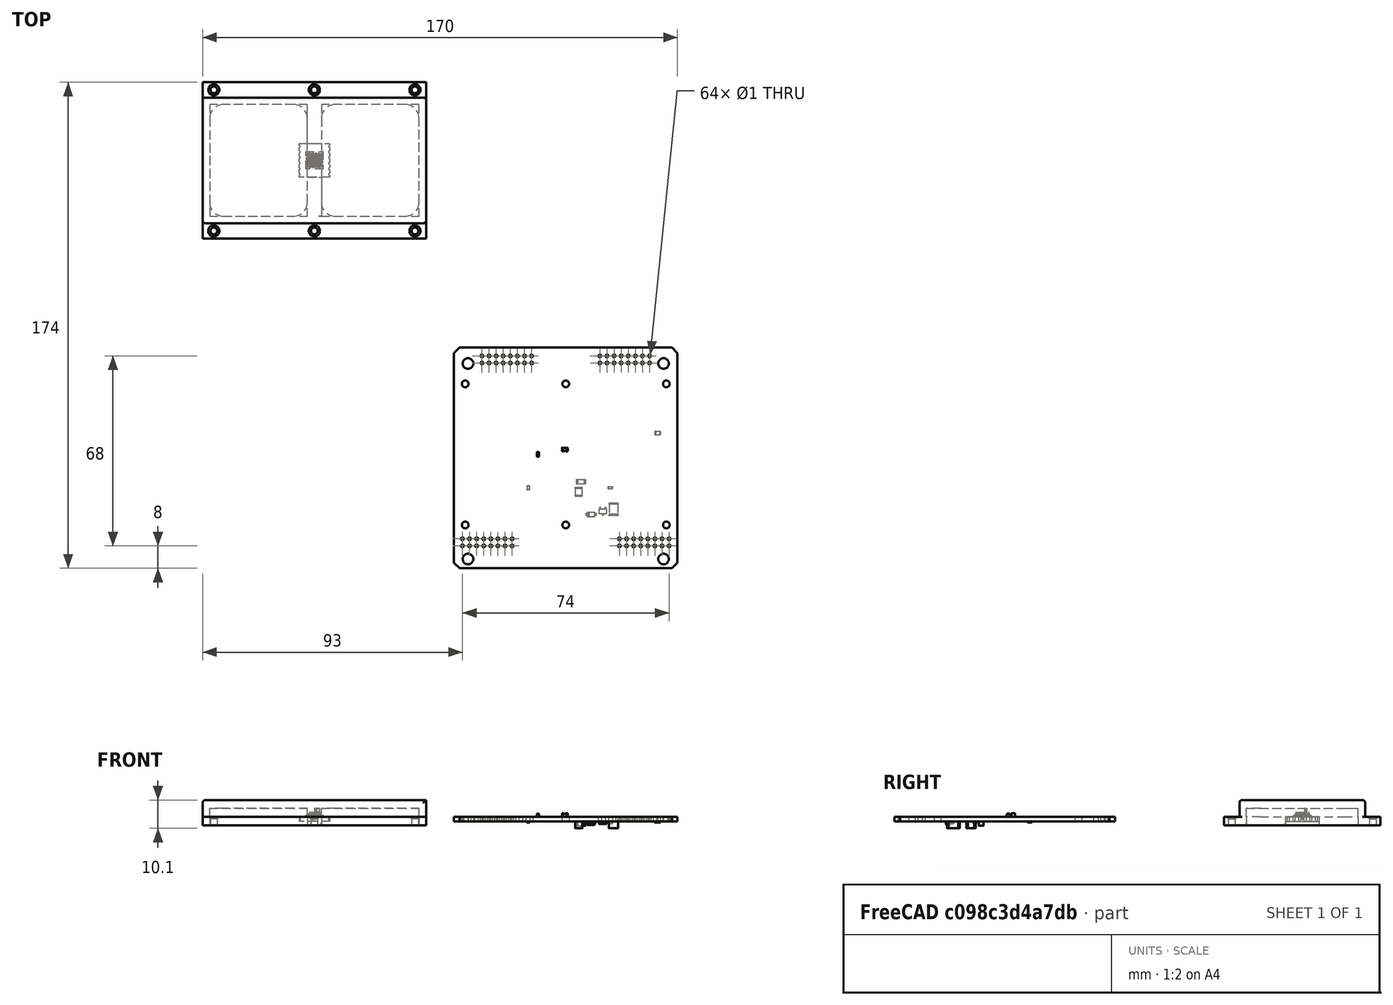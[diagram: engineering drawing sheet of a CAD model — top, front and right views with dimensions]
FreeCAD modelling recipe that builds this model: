
FCSTD DOCUMENT  (FreeCAD 0.21R33771 (Git))
Label: Modelo3DV2
License: All rights reserved
LicenseURL: http://en.wikipedia.org/wiki/All_rights_reserved
objects: Part::Feature×268, App::Link×148, App::Part×28, PartDesign::CoordinateSystem×1, Sketcher::SketchObject×1
note: 270 computed .brp shape members not serialized (recipe doc carries the construction recipe); baked Part::Feature solids carry a one-line shape summary decoded from their .brp

FEATURE [PartDesign::CoordinateSystem] Local_CS_d980
  AttacherType = Attacher::AttachEngine3D
  MapMode = 2
  Support = -> [X_Axis001]
FEATURE [Part::Feature] Pcb_d980
  shape: bbox 80 x 79 x 1.6 mm, 84 faces (baked)
FEATURE [Sketcher::SketchObject] PCB_Sketch_d980
  FullyConstrained = false
  sketch-geometry (12):
    g0: LineSegment StartX=52 StartY=-146 StartZ=0 EndX=50 EndY=-144 EndZ=0
    g1: LineSegment StartX=50 StartY=-69 StartZ=0 EndX=52 EndY=-67 EndZ=0
    g2: LineSegment StartX=50 StartY=-144 StartZ=0 EndX=50 EndY=-69 EndZ=0
    g3: LineSegment StartX=52 StartY=-67 StartZ=0 EndX=128 EndY=-67 EndZ=0
    g4: LineSegment StartX=128 StartY=-146 StartZ=0 EndX=52 EndY=-146 EndZ=0
    g5: LineSegment StartX=128 StartY=-67 StartZ=0 EndX=130 EndY=-69 EndZ=0
    g6: LineSegment StartX=130 StartY=-69 StartZ=0 EndX=130 EndY=-144 EndZ=0
    g7: LineSegment StartX=130 StartY=-144 StartZ=0 EndX=128 EndY=-146 EndZ=0
    g8: Circle CenterX=125 CenterY=-142.7 CenterZ=0 NormalX=0 NormalY=0 NormalZ=1 AngleXU=0 Radius=1.9
    g9: Circle CenterX=55 CenterY=-72.7 CenterZ=0 NormalX=0 NormalY=0 NormalZ=1 AngleXU=0 Radius=1.9
    g10: Circle CenterX=55 CenterY=-142.7 CenterZ=0 NormalX=0 NormalY=0 NormalZ=1 AngleXU=0 Radius=1.9
    g11: Circle CenterX=125 CenterY=-72.7 CenterZ=0 NormalX=0 NormalY=0 NormalZ=1 AngleXU=0 Radius=1.9
  constraints (8):
    c: Coincident(g0,g2)
    c: Coincident(g1,g2)
    c: Coincident(g0,g4)
    c: Coincident(g1,g3)
    c: Coincident(g4,g7)
    c: Coincident(g3,g5)
    c: Coincident(g6,g7)
    c: Coincident(g5,g6)
FEATURE [Part::Feature] Part__Feature  label="BODY-SOT"
  Placement = pos=(0,0,0.9) rot=(0.57735,-0.57735,-0.57735;2.0944rad)
  shape: bbox 1.6 x 2.9 x 1.1 mm, 42 faces (baked)
FEATURE [Part::Feature] Part__Feature001  label="LEAD-SOT"
  Placement = pos=(-0.939537,-0.95,0.25) rot=(0.57735,-0.57735,-0.57735;2.0944rad)
  shape: bbox 0.6 x 0.4 x 0.9 mm, 14 faces (baked)
FEATURE [Part::Feature] Part__Feature002  label="LEAD-SOT001"
  Placement = pos=(-0.939537,0,0.25) rot=(0.57735,-0.57735,-0.57735;2.0944rad)
  shape: bbox 0.6 x 0.4 x 0.9 mm, 14 faces (baked)
FEATURE [Part::Feature] Part__Feature003  label="LEAD-SOT002"
  Placement = pos=(-0.939537,0.95,0.25) rot=(0.57735,-0.57735,-0.57735;2.0944rad)
  shape: bbox 0.6 x 0.4 x 0.9 mm, 14 faces (baked)
FEATURE [Part::Feature] Part__Feature004  label="LEAD-SOT003"
  Placement = pos=(0.939537,-0.95,0.25) rot=(0.57735,0.57735,0.57735;2.0944rad)
  shape: bbox 0.6 x 0.4 x 0.9 mm, 14 faces (baked)
FEATURE [Part::Feature] Part__Feature005  label="LEAD-SOT004"
  Placement = pos=(0.939537,0,0.25) rot=(0.57735,0.57735,0.57735;2.0944rad)
  shape: bbox 0.6 x 0.4 x 0.9 mm, 14 faces (baked)
FEATURE [Part::Feature] Part__Feature006  label="LEAD-SOT005"
  Placement = pos=(0.939537,0.95,0.25) rot=(0.57735,0.57735,0.57735;2.0944rad)
  shape: bbox 0.6 x 0.4 x 0.9 mm, 14 faces (baked)
FEATURE [App::Part] DBV0006A_ASM  label="07_SensorTemperatura.kicad_sch_DBV0006A_ASM_bef77850255a"
  Group = -> [Part__Feature,Part__Feature001,Part__Feature002,Part__Feature003,Part__Feature004,Part__Feature005,Part__Feature006]
  Origin = -> Origin008
  Placement = pos=(89.6348,-106.35,0) rot=(0,0,1;3.14159rad)
FEATURE [Part::Feature] Shape  label="06_PlacasSiPM.kicad_sch_LED_0603_1608Metric_667c60cf1737"
  Placement = pos=(80,-105.25,0) rot=(0,0,-1;1.5708rad)
  shape: bbox 0.8 x 1.6 x 1.1 mm, 50 faces (baked)
FEATURE [Part::Feature] Shape001  label="07_SensorTemperatura.kicad_sch_C_0805_2012Metric_4f3bec8a4ad3"
  Placement = pos=(89.65,-103.5,0) rot=(0,0,1;0rad)
  shape: bbox 2 x 1.25 x 1.25 mm, 28 faces (baked)
FEATURE [Part::Feature] Part__Feature007  label="Centellador_1"
  shape: bbox 35 x 40 x 3 mm, 10 faces (baked)
FEATURE [Part::Feature] Part__Feature008  label="Centellador_2"
  shape: bbox 35 x 40 x 3 mm, 10 faces (baked)
FEATURE [Part::Feature] Part__Feature009  label="Cuerpo"
  shape: bbox 80 x 56 x 9 mm, 65 faces (baked)
FEATURE [App::Part] CentelladorV2  label="06_PlacasSiPM.kicad_sch_CentelladorV2_ad8b2182f1ab"
  Group = -> [Part__Feature007,Part__Feature008,Part__Feature009]
  Origin = -> Origin009
  Placement = pos=(90,-105.25,2.5) rot=(0,0,1;0rad)
FEATURE [App::Link] _6_PlacasSiPM_kicad_sch_LED_0603_1608Metric_667c60cf1737_ln_  label="06_PlacasSiPM.kicad_sch_PlacasSiPM.kicad_sch_LED_0603_1608Metric_7981f1ddc297"
  LinkPlacement = pos=(100,-105.25,0) rot=(0,0,-1;1.5708rad)
  LinkedObject = -> Shape
  Placement = pos=(100,-105.25,0) rot=(0,0,-1;1.5708rad)
FEATURE [Part::Feature] Part__Feature010  label="Pcb_1cf2"
  Placement = pos=(-150.5,123,0) rot=(0,0,1;0rad)
  shape: bbox 11 x 12 x 1.6 mm, 36 faces (baked)
FEATURE [Part::Feature] Part__Feature011  label="topPads_1cf2_cut"
  Placement = pos=(0,0,0.02) rot=(0,0,1;0rad)
  shape: bbox 0.675 x 1.35 x 2e-07 mm, 1 faces, 0 solids (baked)
FEATURE [Part::Feature] Part__Feature012  label="topPads_1cf2_cut001"
  Placement = pos=(0,0,0.02) rot=(0,0,1;0rad)
  shape: bbox 0.675 x 1.35 x 2e-07 mm, 1 faces, 0 solids (baked)
FEATURE [Part::Feature] Part__Feature013  label="topPads_1cf2_cut002"
  Placement = pos=(0,0,0.02) rot=(0,0,1;0rad)
  shape: bbox 0.675 x 1.35 x 2e-07 mm, 1 faces, 0 solids (baked)
FEATURE [Part::Feature] Part__Feature014  label="topPads_1cf2_cut003"
  Placement = pos=(0,0,0.02) rot=(0,0,1;0rad)
  shape: bbox 0.675 x 1.35 x 2e-07 mm, 1 faces, 0 solids (baked)
FEATURE [Part::Feature] Part__Feature015  label="topPads_1cf2_cut004"
  Placement = pos=(0,0,0.02) rot=(0,0,1;0rad)
  shape: bbox 0.675 x 1.35 x 2e-07 mm, 1 faces, 0 solids (baked)
FEATURE [Part::Feature] Part__Feature016  label="topPads_1cf2_cut005"
  Placement = pos=(0,0,0.02) rot=(0,0,1;0rad)
  shape: bbox 0.675 x 1.35 x 2e-07 mm, 1 faces, 0 solids (baked)
FEATURE [Part::Feature] Part__Feature017  label="topPads_1cf2_cut006"
  Placement = pos=(0,0,0.02) rot=(0,0,1;0rad)
  shape: bbox 0.675 x 1.35 x 2e-07 mm, 1 faces, 0 solids (baked)
FEATURE [Part::Feature] Part__Feature018  label="topPads_1cf2_cut007"
  Placement = pos=(0,0,0.02) rot=(0,0,1;0rad)
  shape: bbox 0.675 x 1.35 x 2e-07 mm, 1 faces, 0 solids (baked)
FEATURE [Part::Feature] Part__Feature019  label="topPads_1cf2_cut008"
  Placement = pos=(0,0,0.02) rot=(0,0,1;0rad)
  shape: bbox 0.675 x 1.35 x 2e-07 mm, 1 faces, 0 solids (baked)
FEATURE [Part::Feature] Part__Feature020  label="topPads_1cf2_cut009"
  Placement = pos=(0,0,0.02) rot=(0,0,1;0rad)
  shape: bbox 0.675 x 1.35 x 2e-07 mm, 1 faces, 0 solids (baked)
FEATURE [Part::Feature] Part__Feature021  label="topPads_1cf2_cut010"
  Placement = pos=(0,0,0.02) rot=(0,0,1;0rad)
  shape: bbox 0.675 x 1.35 x 2e-07 mm, 1 faces, 0 solids (baked)
FEATURE [Part::Feature] Part__Feature022  label="topPads_1cf2_cut011"
  Placement = pos=(0,0,0.02) rot=(0,0,1;0rad)
  shape: bbox 0.675 x 1.35 x 2e-07 mm, 1 faces, 0 solids (baked)
FEATURE [Part::Feature] Part__Feature023  label="topPads_1cf2_cut012"
  Placement = pos=(0,0,0.02) rot=(0,0,1;0rad)
  shape: bbox 0.6 x 0.6 x 2e-07 mm, 1 faces, 0 solids (baked)
FEATURE [Part::Feature] Part__Feature024  label="topPads_1cf2_cut013"
  Placement = pos=(0,0,0.02) rot=(0,0,1;0rad)
  shape: bbox 0.6 x 0.6 x 2e-07 mm, 1 faces, 0 solids (baked)
FEATURE [Part::Feature] Part__Feature025  label="topPads_1cf2_cut014"
  Placement = pos=(0,0,0.02) rot=(0,0,1;0rad)
  shape: bbox 0.6 x 0.6 x 2e-07 mm, 1 faces, 0 solids (baked)
FEATURE [Part::Feature] Part__Feature026  label="topPads_1cf2_cut015"
  Placement = pos=(0,0,0.02) rot=(0,0,1;0rad)
  shape: bbox 0.6 x 0.6 x 2e-07 mm, 1 faces, 0 solids (baked)
FEATURE [Part::Feature] Part__Feature027  label="topPads_1cf2_cut016"
  Placement = pos=(0,0,0.02) rot=(0,0,1;0rad)
  shape: bbox 0.6 x 0.6 x 2e-07 mm, 1 faces, 0 solids (baked)
FEATURE [Part::Feature] Part__Feature028  label="topPads_1cf2_cut017"
  Placement = pos=(0,0,0.02) rot=(0,0,1;0rad)
  shape: bbox 0.6 x 0.6 x 2e-07 mm, 1 faces, 0 solids (baked)
FEATURE [Part::Feature] Part__Feature029  label="topPads_1cf2_cut018"
  Placement = pos=(0,0,0.02) rot=(0,0,1;0rad)
  shape: bbox 0.2032 x 0.2032 x 2e-07 mm, 1 faces, 0 solids (baked)
FEATURE [Part::Feature] Part__Feature030  label="topPads_1cf2_cut019"
  Placement = pos=(0,0,0.02) rot=(0,0,1;0rad)
  shape: bbox 0.2032 x 0.2032 x 2e-07 mm, 1 faces, 0 solids (baked)
FEATURE [Part::Feature] Part__Feature031  label="topPads_1cf2_cut020"
  Placement = pos=(0,0,0.02) rot=(0,0,1;0rad)
  shape: bbox 0.2032 x 0.2032 x 2e-07 mm, 1 faces, 0 solids (baked)
FEATURE [Part::Feature] Part__Feature032  label="topPads_1cf2_cut021"
  Placement = pos=(0,0,0.02) rot=(0,0,1;0rad)
  shape: bbox 0.2032 x 0.2032 x 2e-07 mm, 1 faces, 0 solids (baked)
FEATURE [Part::Feature] Part__Feature033  label="topPads_1cf2_cut022"
  Placement = pos=(0,0,0.02) rot=(0,0,1;0rad)
  shape: bbox 0.2032 x 0.2032 x 2e-07 mm, 1 faces, 0 solids (baked)
FEATURE [Part::Feature] Part__Feature034  label="topPads_1cf2_cut023"
  Placement = pos=(0,0,0.02) rot=(0,0,1;0rad)
  shape: bbox 0.2032 x 0.2032 x 2e-07 mm, 1 faces, 0 solids (baked)
FEATURE [Part::Feature] Part__Feature035  label="topPads_1cf2_cut024"
  Placement = pos=(0,0,0.02) rot=(0,0,1;0rad)
  shape: bbox 0.2032 x 0.2032 x 2e-07 mm, 1 faces, 0 solids (baked)
FEATURE [Part::Feature] Part__Feature036  label="topPads_1cf2_cut025"
  Placement = pos=(0,0,0.02) rot=(0,0,1;0rad)
  shape: bbox 0.2032 x 0.2032 x 2e-07 mm, 1 faces, 0 solids (baked)
FEATURE [Part::Feature] Part__Feature037  label="topPads_1cf2_cut026"
  Placement = pos=(0,0,0.02) rot=(0,0,1;0rad)
  shape: bbox 0.2032 x 0.2032 x 2e-07 mm, 1 faces, 0 solids (baked)
FEATURE [Part::Feature] Part__Feature038  label="topPads_1cf2_cut027"
  Placement = pos=(0,0,0.02) rot=(0,0,1;0rad)
  shape: bbox 0.2032 x 0.2032 x 2e-07 mm, 1 faces, 0 solids (baked)
FEATURE [Part::Feature] Part__Feature039  label="topPads_1cf2_cut028"
  Placement = pos=(0,0,0.02) rot=(0,0,1;0rad)
  shape: bbox 0.2032 x 0.2032 x 2e-07 mm, 1 faces, 0 solids (baked)
FEATURE [Part::Feature] Part__Feature040  label="topPads_1cf2_cut029"
  Placement = pos=(0,0,0.02) rot=(0,0,1;0rad)
  shape: bbox 0.2032 x 0.2032 x 2e-07 mm, 1 faces, 0 solids (baked)
FEATURE [Part::Feature] Part__Feature041  label="topPads_1cf2_cut030"
  Placement = pos=(0,0,0.02) rot=(0,0,1;0rad)
  shape: bbox 0.2032 x 0.2032 x 2e-07 mm, 1 faces, 0 solids (baked)
FEATURE [Part::Feature] Part__Feature042  label="topPads_1cf2_cut031"
  Placement = pos=(0,0,0.02) rot=(0,0,1;0rad)
  shape: bbox 0.2032 x 0.2032 x 2e-07 mm, 1 faces, 0 solids (baked)
FEATURE [Part::Feature] Part__Feature043  label="topPads_1cf2_cut032"
  Placement = pos=(0,0,0.02) rot=(0,0,1;0rad)
  shape: bbox 0.2032 x 0.2032 x 2e-07 mm, 1 faces, 0 solids (baked)
FEATURE [Part::Feature] Part__Feature044  label="topPads_1cf2_cut033"
  Placement = pos=(0,0,0.02) rot=(0,0,1;0rad)
  shape: bbox 0.2032 x 0.2032 x 2e-07 mm, 1 faces, 0 solids (baked)
FEATURE [Part::Feature] Part__Feature045  label="topPads_1cf2_cut034"
  Placement = pos=(0,0,0.02) rot=(0,0,1;0rad)
  shape: bbox 0.2032 x 0.2032 x 2e-07 mm, 1 faces, 0 solids (baked)
FEATURE [Part::Feature] Part__Feature046  label="topPads_1cf2_cut035"
  Placement = pos=(0,0,0.02) rot=(0,0,1;0rad)
  shape: bbox 0.2032 x 0.2032 x 2e-07 mm, 1 faces, 0 solids (baked)
FEATURE [Part::Feature] Part__Feature047  label="topPads_1cf2_cut036"
  Placement = pos=(0,0,0.02) rot=(0,0,1;0rad)
  shape: bbox 0.2032 x 0.2032 x 2e-07 mm, 1 faces, 0 solids (baked)
FEATURE [Part::Feature] Part__Feature048  label="topPads_1cf2_cut037"
  Placement = pos=(0,0,0.02) rot=(0,0,1;0rad)
  shape: bbox 0.2032 x 0.2032 x 2e-07 mm, 1 faces, 0 solids (baked)
FEATURE [Part::Feature] Part__Feature049  label="topPads_1cf2_cut038"
  Placement = pos=(0,0,0.02) rot=(0,0,1;0rad)
  shape: bbox 0.2032 x 0.2032 x 2e-07 mm, 1 faces, 0 solids (baked)
FEATURE [Part::Feature] Part__Feature050  label="topPads_1cf2_cut039"
  Placement = pos=(0,0,0.02) rot=(0,0,1;0rad)
  shape: bbox 0.2032 x 0.2032 x 2e-07 mm, 1 faces, 0 solids (baked)
FEATURE [Part::Feature] Part__Feature051  label="topPads_1cf2_cut040"
  Placement = pos=(0,0,0.02) rot=(0,0,1;0rad)
  shape: bbox 0.2032 x 0.2032 x 2e-07 mm, 1 faces, 0 solids (baked)
FEATURE [Part::Feature] Part__Feature052  label="topPads_1cf2_cut041"
  Placement = pos=(0,0,0.02) rot=(0,0,1;0rad)
  shape: bbox 0.2032 x 0.2032 x 2e-07 mm, 1 faces, 0 solids (baked)
FEATURE [Part::Feature] Part__Feature053  label="topPads_1cf2_cut042"
  Placement = pos=(0,0,0.02) rot=(0,0,1;0rad)
  shape: bbox 0.2032 x 0.2032 x 2e-07 mm, 1 faces, 0 solids (baked)
FEATURE [Part::Feature] Part__Feature054  label="topPads_1cf2_cut043"
  Placement = pos=(0,0,0.02) rot=(0,0,1;0rad)
  shape: bbox 0.2032 x 0.2032 x 2e-07 mm, 1 faces, 0 solids (baked)
FEATURE [Part::Feature] Part__Feature055  label="topPads_1cf2_cut044"
  Placement = pos=(0,0,0.02) rot=(0,0,1;0rad)
  shape: bbox 0.2032 x 0.2032 x 2e-07 mm, 1 faces, 0 solids (baked)
FEATURE [Part::Feature] Part__Feature056  label="topPads_1cf2_cut045"
  Placement = pos=(0,0,0.02) rot=(0,0,1;0rad)
  shape: bbox 0.2032 x 0.2032 x 2e-07 mm, 1 faces, 0 solids (baked)
FEATURE [Part::Feature] Part__Feature057  label="topPads_1cf2_cut046"
  Placement = pos=(0,0,0.02) rot=(0,0,1;0rad)
  shape: bbox 0.2032 x 0.2032 x 2e-07 mm, 1 faces, 0 solids (baked)
FEATURE [Part::Feature] Part__Feature058  label="topPads_1cf2_cut047"
  Placement = pos=(0,0,0.02) rot=(0,0,1;0rad)
  shape: bbox 0.2032 x 0.2032 x 2e-07 mm, 1 faces, 0 solids (baked)
FEATURE [Part::Feature] Part__Feature059  label="topPads_1cf2_cut048"
  Placement = pos=(0,0,0.02) rot=(0,0,1;0rad)
  shape: bbox 0.2032 x 0.2032 x 2e-07 mm, 1 faces, 0 solids (baked)
FEATURE [Part::Feature] Part__Feature060  label="topPads_1cf2_cut049"
  Placement = pos=(0,0,0.02) rot=(0,0,1;0rad)
  shape: bbox 0.2032 x 0.2032 x 2e-07 mm, 1 faces, 0 solids (baked)
FEATURE [Part::Feature] Part__Feature061  label="topPads_1cf2_cut050"
  Placement = pos=(0,0,0.02) rot=(0,0,1;0rad)
  shape: bbox 0.2032 x 0.2032 x 2e-07 mm, 1 faces, 0 solids (baked)
FEATURE [Part::Feature] Part__Feature062  label="topPads_1cf2_cut051"
  Placement = pos=(0,0,0.02) rot=(0,0,1;0rad)
  shape: bbox 0.2032 x 0.2032 x 2e-07 mm, 1 faces, 0 solids (baked)
FEATURE [Part::Feature] Part__Feature063  label="topPads_1cf2_cut052"
  Placement = pos=(0,0,0.02) rot=(0,0,1;0rad)
  shape: bbox 0.2032 x 0.2032 x 2e-07 mm, 1 faces, 0 solids (baked)
FEATURE [Part::Feature] Part__Feature064  label="topPads_1cf2_cut053"
  Placement = pos=(0,0,0.02) rot=(0,0,1;0rad)
  shape: bbox 0.2032 x 0.2032 x 2e-07 mm, 1 faces, 0 solids (baked)
FEATURE [App::Part] topPads_1cf2_cut  label="topPads_1cf2_cut054"
  Group = -> [Part__Feature011,Part__Feature012,Part__Feature013,Part__Feature014,Part__Feature015,Part__Feature016,Part__Feature017,Part__Feature018,Part__Feature019,Part__Feature020,Part__Feature021,Part__Feature022,Part__Feature023,Part__Feature024,Part__Feature025,Part__Feature026,Part__Feature027,Part__Feature028,Part__Feature029,Part__Feature030,Part__Feature031,Part__Feature032,Part__Feature033,+31 more]
  Origin = -> Origin010
FEATURE [Part::Feature] Part__Feature065  label="topTracks_1cf2"
  Placement = pos=(-150.5,123,0.01) rot=(0,0,1;0rad)
  shape: bbox 0.8 x 2.3 x 2e-07 mm, 1 faces, 0 solids (baked)
FEATURE [Part::Feature] Part__Feature066  label="topTracks_1cf003"
  Placement = pos=(-150.5,123,0.01) rot=(0,0,1;0rad)
  shape: bbox 1.492 x 0.9917 x 2e-07 mm, 1 faces, 0 solids (baked)
FEATURE [Part::Feature] Part__Feature067  label="topTracks_1cf004"
  Placement = pos=(-150.5,123,0.01) rot=(0,0,1;0rad)
  shape: bbox 1.492 x 0.9917 x 2e-07 mm, 1 faces, 0 solids (baked)
FEATURE [Part::Feature] Part__Feature068  label="topTracks_1cf005"
  Placement = pos=(-150.5,123,0.01) rot=(0,0,1;0rad)
  shape: bbox 0.6917 x 1.592 x 2e-07 mm, 1 faces, 0 solids (baked)
FEATURE [Part::Feature] Part__Feature069  label="topTracks_1cf006"
  Placement = pos=(-150.5,123,0.01) rot=(0,0,1;0rad)
  shape: bbox 1.492 x 0.5917 x 2e-07 mm, 1 faces, 0 solids (baked)
FEATURE [Part::Feature] Part__Feature070  label="topTracks_1cf007"
  Placement = pos=(-150.5,123,0.01) rot=(0,0,1;0rad)
  shape: bbox 1.492 x 0.5917 x 2e-07 mm, 1 faces, 0 solids (baked)
FEATURE [Part::Feature] Part__Feature071  label="topTracks_1cf008"
  Placement = pos=(-150.5,123,0.01) rot=(0,0,1;0rad)
  shape: bbox 0.1969 x 0.1969 x 2e-07 mm, 1 faces, 0 solids (baked)
FEATURE [App::Part] topTracks_1cf2  label="topTracks_1cf009"
  Group = -> [Part__Feature065,Part__Feature066,Part__Feature067,Part__Feature068,Part__Feature069,Part__Feature070,Part__Feature071]
  Origin = -> Origin011
FEATURE [Part::Feature] Part__Feature072  label="topZones_1cf2"
  Placement = pos=(-150.5,123,0.01) rot=(0,0,1;0rad)
  shape: bbox 10.7 x 12.05 x 2e-07 mm, 1 faces, 0 solids (baked)
FEATURE [Part::Feature] Part__Feature073  label="botPads_1cf2_cut"
  Placement = pos=(0,0,-1.62) rot=(0,0,1;0rad)
  shape: bbox 0.675 x 1.35 x 2e-07 mm, 1 faces, 0 solids (baked)
FEATURE [Part::Feature] Part__Feature074  label="botPads_1cf2_cut001"
  Placement = pos=(0,0,-1.62) rot=(0,0,1;0rad)
  shape: bbox 0.675 x 1.35 x 2e-07 mm, 1 faces, 0 solids (baked)
FEATURE [Part::Feature] Part__Feature075  label="botPads_1cf2_cut002"
  Placement = pos=(0,0,-1.62) rot=(0,0,1;0rad)
  shape: bbox 0.675 x 1.35 x 2e-07 mm, 1 faces, 0 solids (baked)
FEATURE [Part::Feature] Part__Feature076  label="botPads_1cf2_cut003"
  Placement = pos=(0,0,-1.62) rot=(0,0,1;0rad)
  shape: bbox 0.675 x 1.35 x 2e-07 mm, 1 faces, 0 solids (baked)
FEATURE [Part::Feature] Part__Feature077  label="botPads_1cf2_cut004"
  Placement = pos=(0,0,-1.62) rot=(0,0,1;0rad)
  shape: bbox 0.675 x 1.35 x 2e-07 mm, 1 faces, 0 solids (baked)
FEATURE [Part::Feature] Part__Feature078  label="botPads_1cf2_cut005"
  Placement = pos=(0,0,-1.62) rot=(0,0,1;0rad)
  shape: bbox 0.675 x 1.35 x 2e-07 mm, 1 faces, 0 solids (baked)
FEATURE [Part::Feature] Part__Feature079  label="botPads_1cf2_cut006"
  Placement = pos=(0,0,-1.62) rot=(0,0,1;0rad)
  shape: bbox 0.675 x 1.35 x 2e-07 mm, 1 faces, 0 solids (baked)
FEATURE [Part::Feature] Part__Feature080  label="botPads_1cf2_cut007"
  Placement = pos=(0,0,-1.62) rot=(0,0,1;0rad)
  shape: bbox 0.675 x 1.35 x 2e-07 mm, 1 faces, 0 solids (baked)
FEATURE [Part::Feature] Part__Feature081  label="botPads_1cf2_cut008"
  Placement = pos=(0,0,-1.62) rot=(0,0,1;0rad)
  shape: bbox 0.675 x 1.35 x 2e-07 mm, 1 faces, 0 solids (baked)
FEATURE [Part::Feature] Part__Feature082  label="botPads_1cf2_cut009"
  Placement = pos=(0,0,-1.62) rot=(0,0,1;0rad)
  shape: bbox 0.675 x 1.35 x 2e-07 mm, 1 faces, 0 solids (baked)
FEATURE [Part::Feature] Part__Feature083  label="botPads_1cf2_cut010"
  Placement = pos=(0,0,-1.62) rot=(0,0,1;0rad)
  shape: bbox 0.675 x 1.35 x 2e-07 mm, 1 faces, 0 solids (baked)
FEATURE [Part::Feature] Part__Feature084  label="botPads_1cf2_cut011"
  Placement = pos=(0,0,-1.62) rot=(0,0,1;0rad)
  shape: bbox 0.675 x 1.35 x 2e-07 mm, 1 faces, 0 solids (baked)
FEATURE [Part::Feature] Part__Feature085  label="botPads_1cf2_cut012"
  Placement = pos=(0,0,-1.62) rot=(0,0,1;0rad)
  shape: bbox 0.6 x 0.6 x 2e-07 mm, 1 faces, 0 solids (baked)
FEATURE [Part::Feature] Part__Feature086  label="botPads_1cf2_cut013"
  Placement = pos=(0,0,-1.62) rot=(0,0,1;0rad)
  shape: bbox 0.6 x 0.6 x 2e-07 mm, 1 faces, 0 solids (baked)
FEATURE [Part::Feature] Part__Feature087  label="botPads_1cf2_cut014"
  Placement = pos=(0,0,-1.62) rot=(0,0,1;0rad)
  shape: bbox 0.6 x 0.6 x 2e-07 mm, 1 faces, 0 solids (baked)
FEATURE [Part::Feature] Part__Feature088  label="botPads_1cf2_cut015"
  Placement = pos=(0,0,-1.62) rot=(0,0,1;0rad)
  shape: bbox 0.6 x 0.6 x 2e-07 mm, 1 faces, 0 solids (baked)
FEATURE [Part::Feature] Part__Feature089  label="botPads_1cf2_cut016"
  Placement = pos=(0,0,-1.62) rot=(0,0,1;0rad)
  shape: bbox 0.6 x 0.6 x 2e-07 mm, 1 faces, 0 solids (baked)
FEATURE [Part::Feature] Part__Feature090  label="botPads_1cf2_cut017"
  Placement = pos=(0,0,-1.62) rot=(0,0,1;0rad)
  shape: bbox 0.6 x 0.6 x 2e-07 mm, 1 faces, 0 solids (baked)
FEATURE [App::Part] botPads_1cf2_cut  label="botPads_1cf2_cut018"
  Group = -> [Part__Feature073,Part__Feature074,Part__Feature075,Part__Feature076,Part__Feature077,Part__Feature078,Part__Feature079,Part__Feature080,Part__Feature081,Part__Feature082,Part__Feature083,Part__Feature084,Part__Feature085,Part__Feature086,Part__Feature087,Part__Feature088,Part__Feature089,Part__Feature090]
  Origin = -> Origin012
FEATURE [Part::Feature] Part__Feature091  label="botTracks_1cf2"
  Placement = pos=(-150.5,123,-1.61) rot=(0,0,1;0rad)
  shape: bbox 9.113 x 5.6 x 2e-07 mm, 1 faces, 0 solids (baked)
FEATURE [Part::Feature] Part__Feature092  label="botTracks_1cf003"
  Placement = pos=(-150.5,123,-1.61) rot=(0,0,1;0rad)
  shape: bbox 1.297 x 3.297 x 2e-07 mm, 1 faces, 0 solids (baked)
FEATURE [App::Part] botTracks_1cf2  label="botTracks_1cf004"
  Group = -> [Part__Feature091,Part__Feature092]
  Origin = -> Origin013
FEATURE [App::Part] Board_Geoms_1cf2
  Group = -> [Part__Feature010,topPads_1cf2_cut,topTracks_1cf2,Part__Feature072,botPads_1cf2_cut,botTracks_1cf2]
  Origin = -> Origin014
FEATURE [Part::Feature] Part__Feature093  label="part"
  shape: bbox 0.254 x 0.254 x 0.254 mm, 1 faces (baked)
FEATURE [Part::Feature] Part__Feature094  label="part001"
  shape: bbox 0.254 x 0.254 x 0.254 mm, 1 faces (baked)
FEATURE [Part::Feature] Part__Feature095  label="part002"
  shape: bbox 0.254 x 0.254 x 0.254 mm, 1 faces (baked)
FEATURE [Part::Feature] Part__Feature096  label="part003"
  shape: bbox 0.254 x 0.254 x 0.254 mm, 1 faces (baked)
FEATURE [Part::Feature] Part__Feature097  label="part004"
  shape: bbox 0.254 x 0.254 x 0.254 mm, 1 faces (baked)
FEATURE [Part::Feature] Part__Feature098  label="part005"
  shape: bbox 0.254 x 0.254 x 0.254 mm, 1 faces (baked)
FEATURE [Part::Feature] Part__Feature099  label="part006"
  shape: bbox 0.254 x 0.254 x 0.254 mm, 1 faces (baked)
FEATURE [Part::Feature] Part__Feature100  label="part007"
  shape: bbox 0.254 x 0.254 x 0.254 mm, 1 faces (baked)
FEATURE [Part::Feature] Part__Feature101  label="part008"
  shape: bbox 0.254 x 0.254 x 0.254 mm, 1 faces (baked)
FEATURE [Part::Feature] Part__Feature102  label="part009"
  shape: bbox 0.254 x 0.254 x 0.254 mm, 1 faces (baked)
FEATURE [Part::Feature] Part__Feature103  label="part010"
  shape: bbox 0.254 x 0.254 x 0.254 mm, 1 faces (baked)
FEATURE [Part::Feature] Part__Feature104  label="part011"
  shape: bbox 0.254 x 0.254 x 0.254 mm, 1 faces (baked)
FEATURE [Part::Feature] Part__Feature105  label="part012"
  shape: bbox 0.254 x 0.254 x 0.254 mm, 1 faces (baked)
FEATURE [Part::Feature] Part__Feature106  label="part013"
  shape: bbox 0.254 x 0.254 x 0.254 mm, 1 faces (baked)
FEATURE [Part::Feature] Part__Feature107  label="part014"
  shape: bbox 0.254 x 0.254 x 0.254 mm, 1 faces (baked)
FEATURE [Part::Feature] Part__Feature108  label="part015"
  shape: bbox 0.254 x 0.254 x 0.254 mm, 1 faces (baked)
FEATURE [Part::Feature] Part__Feature109  label="part016"
  shape: bbox 0.254 x 0.254 x 0.254 mm, 1 faces (baked)
FEATURE [Part::Feature] Part__Feature110  label="part017"
  shape: bbox 0.254 x 0.254 x 0.254 mm, 1 faces (baked)
FEATURE [Part::Feature] Part__Feature111  label="part018"
  shape: bbox 0.254 x 0.254 x 0.254 mm, 1 faces (baked)
FEATURE [Part::Feature] Part__Feature112  label="part019"
  shape: bbox 0.254 x 0.254 x 0.254 mm, 1 faces (baked)
FEATURE [Part::Feature] Part__Feature113  label="part020"
  shape: bbox 0.254 x 0.254 x 0.254 mm, 1 faces (baked)
FEATURE [Part::Feature] Part__Feature114  label="part021"
  shape: bbox 0.254 x 0.254 x 0.254 mm, 1 faces (baked)
FEATURE [Part::Feature] Part__Feature115  label="part022"
  shape: bbox 0.254 x 0.254 x 0.254 mm, 1 faces (baked)
FEATURE [Part::Feature] Part__Feature116  label="part023"
  shape: bbox 0.254 x 0.254 x 0.254 mm, 1 faces (baked)
FEATURE [Part::Feature] Part__Feature117  label="part024"
  shape: bbox 0.254 x 0.254 x 0.254 mm, 1 faces (baked)
FEATURE [Part::Feature] Part__Feature118  label="part025"
  shape: bbox 0.254 x 0.254 x 0.254 mm, 1 faces (baked)
FEATURE [Part::Feature] Part__Feature119  label="part026"
  shape: bbox 0.254 x 0.254 x 0.254 mm, 1 faces (baked)
FEATURE [Part::Feature] Part__Feature120  label="part027"
  shape: bbox 0.254 x 0.254 x 0.254 mm, 1 faces (baked)
FEATURE [Part::Feature] Part__Feature121  label="part028"
  shape: bbox 0.254 x 0.254 x 0.254 mm, 1 faces (baked)
FEATURE [Part::Feature] Part__Feature122  label="part029"
  shape: bbox 0.254 x 0.254 x 0.254 mm, 1 faces (baked)
FEATURE [Part::Feature] Part__Feature123  label="part030"
  shape: bbox 0.254 x 0.254 x 0.254 mm, 1 faces (baked)
FEATURE [Part::Feature] Part__Feature124  label="part031"
  shape: bbox 0.254 x 0.254 x 0.254 mm, 1 faces (baked)
FEATURE [Part::Feature] Part__Feature125  label="part032"
  shape: bbox 0.254 x 0.254 x 0.254 mm, 1 faces (baked)
FEATURE [Part::Feature] Part__Feature126  label="part033"
  shape: bbox 0.254 x 0.254 x 0.254 mm, 1 faces (baked)
FEATURE [Part::Feature] Part__Feature127  label="part034"
  shape: bbox 0.254 x 0.254 x 0.254 mm, 1 faces (baked)
FEATURE [Part::Feature] Part__Feature128  label="part035"
  shape: bbox 0.254 x 0.254 x 0.254 mm, 1 faces (baked)
FEATURE [Part::Feature] Part__Feature129  label="part036"
  shape: bbox 0.3086 x 0.3086 x 0.003 mm, 3 faces (baked)
FEATURE [Part::Feature] Part__Feature130  label="part037"
  shape: bbox 6.172 x 6.172 x 0.407 mm, 6 faces (baked)
FEATURE [App::Part] Placa_SiPM_kicad_sch_part038_7e5b207e7f31  label="Placa_SiPM.kicad_sch_part038_7e5b207e7f31"
  Group = -> [Part__Feature093,Part__Feature094,Part__Feature095,Part__Feature096,Part__Feature097,Part__Feature098,Part__Feature099,Part__Feature100,Part__Feature101,Part__Feature102,Part__Feature103,Part__Feature104,Part__Feature105,Part__Feature106,Part__Feature107,Part__Feature108,Part__Feature109,Part__Feature110,Part__Feature111,Part__Feature112,Part__Feature113,Part__Feature114,Part__Feature115,+15 more]
  Origin = -> Origin015
FEATURE [App::Part] Top_1cf2
  Group = -> [Placa_SiPM_kicad_sch_part038_7e5b207e7f31]
  Origin = -> Origin016
FEATURE [App::Part] Step_Models_1cf2
  Group = -> [Top_1cf2]
  Origin = -> Origin017
FEATURE [App::Part] Placa_SiPM  label="06_PlacasSiPM.kicad_sch_Placa_SiPM_8cd53adc4c3a"
  Group = -> [Board_Geoms_1cf2,Step_Models_1cf2]
  Origin = -> Origin018
  Placement = pos=(70,-105.25,1.6) rot=(0,0,1;0rad)
FEATURE [App::Link] _6_PlacasSiPM_kicad_sch_Placa_SiPM_8cd53adc4c3a_ln_  label="06_PlacasSiPM.kicad_sch_PlacasSiPM.kicad_sch_Placa_SiPM_0cbb51f1506e"
  LinkPlacement = pos=(110,-105.25,1.6) rot=(0,0,1;0rad)
  LinkedObject = -> Placa_SiPM
  Placement = pos=(110,-105.25,1.6) rot=(0,0,1;0rad)
FEATURE [App::Part] Top_d980
  Group = -> [DBV0006A_ASM,Shape,Shape001,CentelladorV2,_6_PlacasSiPM_kicad_sch_LED_0603_1608Metric_667c60cf1737_ln_,Placa_SiPM,_6_PlacasSiPM_kicad_sch_Placa_SiPM_8cd53adc4c3a_ln_]
  Origin = -> Origin003
FEATURE [Part::Feature] Shape002  label="01_Polarizacion.kicad_sch_TSOT_23_32137845036f"
  Placement = pos=(103.275,-125.665,-1.6) rot=(0.707107,-0.707107,0;3.14159rad)
  shape: bbox 2.9 x 2.8 x 0.95 mm, 79 faces (baked)
FEATURE [Part::Feature] Shape003  label="04_GenVref.kicad_sch_R_0805_2012Metric_e7e7c0ed52a6"
  Placement = pos=(122.85,-97.568,-1.6) rot=(1,0,0;3.14159rad)
  shape: bbox 2 x 1.2 x 0.45 mm, 26 faces (baked)
FEATURE [Part::Feature] Shape004  label="01_Polarizacion.kicad_sch_R_0603_1608Metric_55dffa615082"
  Placement = pos=(76.525,-117.25,-1.6) rot=(0.707107,-0.707107,0;3.14159rad)
  shape: bbox 0.8 x 1.6 x 0.45 mm, 26 faces (baked)
FEATURE [App::Link] _4_GenVref_kicad_sch_R_0805_2012Metric_e7e7c0ed52a6_ln_  label="03_Comparación.kicad_sch_GenVref.kicad_sch_R_0805_2012Metric_dcaada17983d"
  LinkPlacement = pos=(93.45,-93.75,-1.6) rot=(0.707107,0.707107,0;3.14159rad)
  LinkedObject = -> Shape003
  Placement = pos=(93.45,-93.75,-1.6) rot=(0.707107,0.707107,0;3.14159rad)
FEATURE [Part::Feature] Part__Feature131  label="BODY_MUA08A"
  Placement = pos=(0,0,0.6897) rot=(0.57735,-0.57735,-0.57735;2.0944rad)
  shape: bbox 2.999 x 2.999 x 0.9985 mm, 46 faces (baked)
FEATURE [Part::Feature] Part__Feature132  label="LEAD_MUA08A"
  Placement = pos=(-1.9177,-0.97536,0.254) rot=(0.57735,-0.57735,-0.57735;2.0944rad)
  shape: bbox 0.9525 x 0.3048 x 0.6897 mm, 14 faces (baked)
FEATURE [Part::Feature] Part__Feature133  label="LEAD_MUA08A001"
  Placement = pos=(-1.9177,-0.32512,0.254) rot=(0.57735,-0.57735,-0.57735;2.0944rad)
  shape: bbox 0.9525 x 0.3048 x 0.6897 mm, 14 faces (baked)
FEATURE [Part::Feature] Part__Feature134  label="LEAD_MUA08A002"
  Placement = pos=(-1.9177,0.32512,0.254) rot=(0.57735,-0.57735,-0.57735;2.0944rad)
  shape: bbox 0.9525 x 0.3048 x 0.6897 mm, 14 faces (baked)
FEATURE [Part::Feature] Part__Feature135  label="LEAD_MUA08A003"
  Placement = pos=(-1.9177,0.97536,0.254) rot=(0.57735,-0.57735,-0.57735;2.0944rad)
  shape: bbox 0.9525 x 0.3048 x 0.6897 mm, 14 faces (baked)
FEATURE [Part::Feature] Part__Feature136  label="LEAD_MUA08A004"
  Placement = pos=(1.9177,-0.97536,0.254) rot=(0.57735,0.57735,0.57735;2.0944rad)
  shape: bbox 0.9525 x 0.3048 x 0.6897 mm, 14 faces (baked)
FEATURE [Part::Feature] Part__Feature137  label="LEAD_MUA08A005"
  Placement = pos=(1.9177,-0.32512,0.254) rot=(0.57735,0.57735,0.57735;2.0944rad)
  shape: bbox 0.9525 x 0.3048 x 0.6897 mm, 14 faces (baked)
FEATURE [Part::Feature] Part__Feature138  label="LEAD_MUA08A006"
  Placement = pos=(1.9177,0.32512,0.254) rot=(0.57735,0.57735,0.57735;2.0944rad)
  shape: bbox 0.9525 x 0.3048 x 0.6897 mm, 14 faces (baked)
FEATURE [Part::Feature] Part__Feature139  label="LEAD_MUA08A007"
  Placement = pos=(1.9177,0.97536,0.254) rot=(0.57735,0.57735,0.57735;2.0944rad)
  shape: bbox 0.9525 x 0.3048 x 0.6897 mm, 14 faces (baked)
FEATURE [App::Part] MUA08A_ASM  label="01_Polarizacion.kicad_sch_MUA08A_ASM_555f9891b5ac"
  Group = -> [Part__Feature131,Part__Feature132,Part__Feature133,Part__Feature134,Part__Feature135,Part__Feature136,Part__Feature137,Part__Feature138,Part__Feature139]
  Origin = -> Origin019
  Placement = pos=(78.8633,-134.025,-1.6) rot=(1,0,0;3.14159rad)
FEATURE [Part::Feature] Shape005  label="01_Polarizacion.kicad_sch_C_1206_3216Metric_f1471ee13c61"
  Placement = pos=(95.4,-114.975,-1.6) rot=(1,0,0;3.14159rad)
  shape: bbox 3.2 x 1.6 x 1.6 mm, 28 faces (baked)
FEATURE [App::Link] _7_SensorTemperatura_kicad_sch_C_0805_2012Metric_4f3bec8a4ad3_ln_  label="03_Comparación.kicad_sch_SensorTemperatura.kicad_sch_C_0805_2012Metric_bb25651ed259"
  LinkPlacement = pos=(87.15,-94.5217,-1.6) rot=(0.707107,-0.707107,0;3.14159rad)
  LinkedObject = -> Shape001
  Placement = pos=(87.15,-94.5217,-1.6) rot=(0.707107,-0.707107,0;3.14159rad)
FEATURE [App::Link] _4_GenVref_kicad_sch_R_0805_2012Metric_e7e7c0ed52a6_ln_001  label="01_Polarizacion.kicad_sch_GenVref.kicad_sch_R_0805_2012Metric_055e7035bca4"
  LinkPlacement = pos=(95.65,-133.1,-1.6) rot=(0,1,0;3.14159rad)
  LinkedObject = -> Shape003
  Placement = pos=(95.65,-133.1,-1.6) rot=(0,1,0;3.14159rad)
FEATURE [App::Link] _4_GenVref_kicad_sch_R_0805_2012Metric_e7e7c0ed52a6_ln_002  label="08_MedicionCorriente.kicad_sch_GenVref.kicad_sch_R_0805_2012Metric_8d90b72a5bf4"
  LinkPlacement = pos=(63.3147,-92.6719,-1.6) rot=(0.707107,-0.707107,0;3.14159rad)
  LinkedObject = -> Shape003
  Placement = pos=(63.3147,-92.6719,-1.6) rot=(0.707107,-0.707107,0;3.14159rad)
FEATURE [App::Link] _4_GenVref_kicad_sch_R_0805_2012Metric_e7e7c0ed52a6_ln_003  label="Placa_DetectorParticulas.kicad_sch_GenVref.kicad_sch_R_0805_2012Metric_d41f5b83ae95"
  LinkPlacement = pos=(92.3,-84.95,-1.6) rot=(0.707107,0.707107,0;3.14159rad)
  LinkedObject = -> Shape003
  Placement = pos=(92.3,-84.95,-1.6) rot=(0.707107,0.707107,0;3.14159rad)
FEATURE [App::Link] _7_SensorTemperatura_kicad_sch_C_0805_2012Metric_4f3bec8a4ad3_ln_001  label="01_Polarizacion.kicad_sch_SensorTemperatura.kicad_sch_C_0805_2012Metric_c7f56b1b11b2"
  LinkPlacement = pos=(101.8,-137.1,-1.6) rot=(1,0,0;3.14159rad)
  LinkedObject = -> Shape001
  Placement = pos=(101.8,-137.1,-1.6) rot=(1,0,0;3.14159rad)
FEATURE [Part::Feature] Shape006  label="01_Polarizacion.kicad_sch_D_SOD_123_c84daf4213db"
  Placement = pos=(99.025,-126.775,-1.6) rot=(1,0,0;3.14159rad)
  shape: bbox 3.8 x 1.6 x 1.25 mm, 67 faces (baked)
FEATURE [App::Link] _4_GenVref_kicad_sch_R_0805_2012Metric_e7e7c0ed52a6_ln_004  label="08_MedicionCorriente.kicad_sch_GenVref.kicad_sch_R_0805_2012Metric_9b7ff64fadd9"
  LinkPlacement = pos=(117.375,-91.2,-1.6) rot=(0.707107,0.707107,0;3.14159rad)
  LinkedObject = -> Shape003
  Placement = pos=(117.375,-91.2,-1.6) rot=(0.707107,0.707107,0;3.14159rad)
FEATURE [Part::Feature] Shape007  label="01_Polarizacion.kicad_sch_C_0603_1608Metric_c67edd4d6b6e"
  Placement = pos=(105.9,-117.175,-1.6) rot=(1,0,0;3.14159rad)
  shape: bbox 1.6 x 0.8 x 0.8 mm, 28 faces (baked)
FEATURE [App::Link] _7_SensorTemperatura_kicad_sch_C_0805_2012Metric_4f3bec8a4ad3_ln_002  label="02_Amplificacion.kicad_sch_SensorTemperatura.kicad_sch_C_0805_2012Metric_19082a8ab6bc"
  LinkPlacement = pos=(80.3003,-107.869,-1.6) rot=(0,1,0;3.14159rad)
  LinkedObject = -> Shape001
  Placement = pos=(80.3003,-107.869,-1.6) rot=(0,1,0;3.14159rad)
FEATURE [App::Link] _4_GenVref_kicad_sch_R_0805_2012Metric_e7e7c0ed52a6_ln_005  label="Placa_DetectorParticulas.kicad_sch_GenVref.kicad_sch_R_0805_2012Metric_88ffaab2a4e8"
  LinkPlacement = pos=(80.3,-91.1125,-1.6) rot=(0.707107,0.707107,0;3.14159rad)
  LinkedObject = -> Shape003
  Placement = pos=(80.3,-91.1125,-1.6) rot=(0.707107,0.707107,0;3.14159rad)
FEATURE [App::Link] _7_SensorTemperatura_kicad_sch_C_0805_2012Metric_4f3bec8a4ad3_ln_003  label="02_Amplificacion.kicad_sch_SensorTemperatura.kicad_sch_C_0805_2012Metric_e581be577117"
  LinkPlacement = pos=(102.6,-104.6,-1.6) rot=(0.707107,-0.707107,0;3.14159rad)
  LinkedObject = -> Shape001
  Placement = pos=(102.6,-104.6,-1.6) rot=(0.707107,-0.707107,0;3.14159rad)
FEATURE [Part::Feature] Part__Feature140  label="part038"
  shape: bbox 0.145 x 0.145 x 0.003 mm, 3 faces (baked)
FEATURE [Part::Feature] Part__Feature141  label="part039"
  shape: bbox 2.901 x 1.301 x 1.121 mm, 14 faces (baked)
FEATURE [Part::Feature] Part__Feature142  label="part040"
  shape: bbox 0.513 x 0.672 x 0.562 mm, 14 faces (baked)
FEATURE [Part::Feature] Part__Feature143  label="part041"
  shape: bbox 0.5111 x 0.6711 x 0.5611 mm, 14 faces (baked)
FEATURE [Part::Feature] Part__Feature144  label="part042"
  shape: bbox 0.5111 x 0.6711 x 0.5611 mm, 14 faces (baked)
FEATURE [App::Part] part  label="01_Polarizacion.kicad_sch_part043_50eeabfdbd3f"
  Group = -> [Part__Feature140,Part__Feature141,Part__Feature142,Part__Feature143,Part__Feature144]
  Origin = -> Origin020
  Placement = pos=(95.13,-136.093,-1.6) rot=(0.707107,-0.707107,0;3.14159rad)
FEATURE [App::Link] _4_GenVref_kicad_sch_R_0805_2012Metric_e7e7c0ed52a6_ln_006  label="04_GenVref.kicad_sch_GenVref.kicad_sch_R_0805_2012Metric_99ee876c09b5"
  LinkPlacement = pos=(57.2375,-118.35,-1.6) rot=(1,0,0;3.14159rad)
  LinkedObject = -> Shape003
  Placement = pos=(57.2375,-118.35,-1.6) rot=(1,0,0;3.14159rad)
FEATURE [App::Link] _4_GenVref_kicad_sch_R_0805_2012Metric_e7e7c0ed52a6_ln_007  label="02_Amplificacion.kicad_sch_GenVref.kicad_sch_R_0805_2012Metric_eb8a10d69283"
  LinkPlacement = pos=(80.3178,-101.789,-1.6) rot=(1,0,0;3.14159rad)
  LinkedObject = -> Shape003
  Placement = pos=(80.3178,-101.789,-1.6) rot=(1,0,0;3.14159rad)
FEATURE [App::Link] _7_SensorTemperatura_kicad_sch_C_0805_2012Metric_4f3bec8a4ad3_ln_004  label="03_Comparación.kicad_sch_SensorTemperatura.kicad_sch_C_0805_2012Metric_0c196a01d999"
  LinkPlacement = pos=(97.1717,-90.0717,-1.6) rot=(0.707107,-0.707107,0;3.14159rad)
  LinkedObject = -> Shape001
  Placement = pos=(97.1717,-90.0717,-1.6) rot=(0.707107,-0.707107,0;3.14159rad)
FEATURE [App::Link] _4_GenVref_kicad_sch_R_0805_2012Metric_e7e7c0ed52a6_ln_008  label="06_PlacasSiPM.kicad_sch_GenVref.kicad_sch_R_0805_2012Metric_111589959746"
  LinkPlacement = pos=(55.75,-87.2125,-1.6) rot=(0.707107,0.707107,0;3.14159rad)
  LinkedObject = -> Shape003
  Placement = pos=(55.75,-87.2125,-1.6) rot=(0.707107,0.707107,0;3.14159rad)
FEATURE [App::Link] _7_SensorTemperatura_kicad_sch_C_0805_2012Metric_4f3bec8a4ad3_ln_005  label="08_MedicionCorriente.kicad_sch_SensorTemperatura.kicad_sch_C_0805_2012Metric_3553cda95077"
  LinkPlacement = pos=(63.2647,-96.9594,-1.6) rot=(1,0,0;3.14159rad)
  LinkedObject = -> Shape001
  Placement = pos=(63.2647,-96.9594,-1.6) rot=(1,0,0;3.14159rad)
FEATURE [App::Link] _7_SensorTemperatura_kicad_sch_C_0805_2012Metric_4f3bec8a4ad3_ln_006  label="02_Amplificacion.kicad_sch_SensorTemperatura.kicad_sch_C_0805_2012Metric_72b3d80cd8ed"
  LinkPlacement = pos=(88.1003,-106.369,-1.6) rot=(0.707107,-0.707107,0;3.14159rad)
  LinkedObject = -> Shape001
  Placement = pos=(88.1003,-106.369,-1.6) rot=(0.707107,-0.707107,0;3.14159rad)
FEATURE [App::Link] _4_GenVref_kicad_sch_R_0805_2012Metric_e7e7c0ed52a6_ln_009  label="01_Polarizacion.kicad_sch_GenVref.kicad_sch_R_0805_2012Metric_c6fd1157d9b8"
  LinkPlacement = pos=(91.45,-118.062,-1.6) rot=(0.707107,-0.707107,0;3.14159rad)
  LinkedObject = -> Shape003
  Placement = pos=(91.45,-118.062,-1.6) rot=(0.707107,-0.707107,0;3.14159rad)
FEATURE [Part::Feature] Shape008  label="01_Polarizacion.kicad_sch_L_1210_3225Metric_350fa5c3db90"
  Placement = pos=(94.675,-118.575,-1.6) rot=(0.707107,0.707107,0;3.14159rad)
  shape: bbox 2.5 x 3.2 x 2.5 mm, 28 faces (baked)
FEATURE [App::Link] _4_GenVref_kicad_sch_R_0805_2012Metric_e7e7c0ed52a6_ln_010  label="01_Polarizacion.kicad_sch_GenVref.kicad_sch_R_0805_2012Metric_a1759b9fb863"
  LinkPlacement = pos=(66.9,-122.8,-1.6) rot=(1,0,0;3.14159rad)
  LinkedObject = -> Shape003
  Placement = pos=(66.9,-122.8,-1.6) rot=(1,0,0;3.14159rad)
FEATURE [Part::Feature] Part__Feature145  label="part043"
  shape: bbox 0.1295 x 0.1295 x 0.002 mm, 3 faces (baked)
FEATURE [Part::Feature] Part__Feature146  label="part044"
  shape: bbox 2.59 x 4.598 x 0.94 mm, 6 faces (baked)
FEATURE [Part::Feature] Part__Feature147  label="part045"
  shape: bbox 0.304 x 0.508 x 0.051 mm, 6 faces (baked)
FEATURE [Part::Feature] Part__Feature148  label="part046"
  shape: bbox 0.508 x 0.304 x 0.051 mm, 6 faces (baked)
FEATURE [Part::Feature] Part__Feature149  label="part047"
  shape: bbox 0.508 x 0.304 x 0.051 mm, 6 faces (baked)
FEATURE [Part::Feature] Part__Feature150  label="part048"
  shape: bbox 0.508 x 0.304 x 0.051 mm, 6 faces (baked)
FEATURE [Part::Feature] Part__Feature151  label="part049"
  shape: bbox 0.508 x 0.304 x 0.051 mm, 6 faces (baked)
FEATURE [Part::Feature] Part__Feature152  label="part050"
  shape: bbox 0.508 x 0.304 x 0.051 mm, 6 faces (baked)
FEATURE [Part::Feature] Part__Feature153  label="part051"
  shape: bbox 0.508 x 0.304 x 0.051 mm, 6 faces (baked)
FEATURE [Part::Feature] Part__Feature154  label="part052"
  shape: bbox 0.508 x 0.304 x 0.051 mm, 6 faces (baked)
FEATURE [Part::Feature] Part__Feature155  label="part053"
  shape: bbox 0.508 x 0.304 x 0.051 mm, 6 faces (baked)
FEATURE [Part::Feature] Part__Feature156  label="part054"
  shape: bbox 0.304 x 0.508 x 0.051 mm, 6 faces (baked)
FEATURE [Part::Feature] Part__Feature157  label="part055"
  shape: bbox 0.304 x 0.508 x 0.051 mm, 6 faces (baked)
FEATURE [Part::Feature] Part__Feature158  label="part056"
  shape: bbox 0.508 x 0.304 x 0.051 mm, 6 faces (baked)
FEATURE [Part::Feature] Part__Feature159  label="part057"
  shape: bbox 0.508 x 0.304 x 0.051 mm, 6 faces (baked)
FEATURE [Part::Feature] Part__Feature160  label="part058"
  shape: bbox 0.508 x 0.304 x 0.051 mm, 6 faces (baked)
FEATURE [Part::Feature] Part__Feature161  label="part059"
  shape: bbox 0.508 x 0.304 x 0.051 mm, 6 faces (baked)
FEATURE [Part::Feature] Part__Feature162  label="part060"
  shape: bbox 0.508 x 0.304 x 0.051 mm, 6 faces (baked)
FEATURE [Part::Feature] Part__Feature163  label="part061"
  shape: bbox 0.508 x 0.304 x 0.051 mm, 6 faces (baked)
FEATURE [Part::Feature] Part__Feature164  label="part062"
  shape: bbox 0.508 x 0.304 x 0.051 mm, 6 faces (baked)
FEATURE [Part::Feature] Part__Feature165  label="part063"
  shape: bbox 0.508 x 0.304 x 0.051 mm, 6 faces (baked)
FEATURE [Part::Feature] Part__Feature166  label="part064"
  shape: bbox 0.304 x 0.508 x 0.051 mm, 6 faces (baked)
FEATURE [Part::Feature] Part__Feature167  label="part065"
  shape: bbox 1.144 x 3.15 x 0.051 mm, 6 faces (baked)
FEATURE [App::Part] part001  label="09_AdapVoltajeDigital.kicad_sch_part066_f10ad10a87d3"
  Group = -> [Part__Feature145,Part__Feature146,Part__Feature147,Part__Feature148,Part__Feature149,Part__Feature150,Part__Feature151,Part__Feature152,Part__Feature153,Part__Feature154,Part__Feature155,Part__Feature156,Part__Feature157,Part__Feature158,Part__Feature159,Part__Feature160,Part__Feature161,Part__Feature162,Part__Feature163,Part__Feature164,Part__Feature165,Part__Feature166,Part__Feature167]
  Origin = -> Origin021
  Placement = pos=(115.705,-131.35,-1.6) rot=(0.707107,0.707107,0;3.14159rad)
FEATURE [App::Link] _7_SensorTemperatura_kicad_sch_C_0805_2012Metric_4f3bec8a4ad3_ln_007  label="02_Amplificacion.kicad_sch_SensorTemperatura.kicad_sch_C_0805_2012Metric_774f6370d5cd"
  LinkPlacement = pos=(86.7003,-102.819,-1.6) rot=(0.707107,-0.707107,0;3.14159rad)
  LinkedObject = -> Shape001
  Placement = pos=(86.7003,-102.819,-1.6) rot=(0.707107,-0.707107,0;3.14159rad)
FEATURE [Part::Feature] Part__Feature168  label="part066"
  shape: bbox 0.2045 x 0.2045 x 0.002 mm, 3 faces (baked)
FEATURE [Part::Feature] Part__Feature169  label="part067"
  shape: bbox 4.09 x 4.09 x 0.762 mm, 6 faces (baked)
FEATURE [Part::Feature] Part__Feature170  label="part068"
  shape: bbox 0.661 x 0.356 x 0.051 mm, 6 faces (baked)
FEATURE [Part::Feature] Part__Feature171  label="part069"
  shape: bbox 0.661 x 0.356 x 0.051 mm, 6 faces (baked)
FEATURE [Part::Feature] Part__Feature172  label="part070"
  shape: bbox 0.661 x 0.356 x 0.051 mm, 6 faces (baked)
FEATURE [Part::Feature] Part__Feature173  label="part071"
  shape: bbox 0.356 x 0.661 x 0.051 mm, 6 faces (baked)
FEATURE [Part::Feature] Part__Feature174  label="part072"
  shape: bbox 0.356 x 0.661 x 0.051 mm, 6 faces (baked)
FEATURE [Part::Feature] Part__Feature175  label="part073"
  shape: bbox 0.356 x 0.661 x 0.051 mm, 6 faces (baked)
FEATURE [Part::Feature] Part__Feature176  label="part074"
  shape: bbox 0.661 x 0.356 x 0.051 mm, 6 faces (baked)
FEATURE [Part::Feature] Part__Feature177  label="part075"
  shape: bbox 0.661 x 0.356 x 0.051 mm, 6 faces (baked)
FEATURE [Part::Feature] Part__Feature178  label="part076"
  shape: bbox 0.661 x 0.356 x 0.051 mm, 6 faces (baked)
FEATURE [Part::Feature] Part__Feature179  label="part077"
  shape: bbox 0.356 x 0.661 x 0.051 mm, 6 faces (baked)
FEATURE [Part::Feature] Part__Feature180  label="part078"
  shape: bbox 0.356 x 0.661 x 0.051 mm, 6 faces (baked)
FEATURE [Part::Feature] Part__Feature181  label="part079"
  shape: bbox 0.356 x 0.661 x 0.051 mm, 6 faces (baked)
FEATURE [Part::Feature] Part__Feature182  label="part080"
  shape: bbox 2.26 x 2.26 x 0.051 mm, 6 faces (baked)
FEATURE [App::Part] part002  label="01_Polarizacion.kicad_sch_part081_0638eee03de4"
  Group = -> [Part__Feature168,Part__Feature169,Part__Feature170,Part__Feature171,Part__Feature172,Part__Feature173,Part__Feature174,Part__Feature175,Part__Feature176,Part__Feature177,Part__Feature178,Part__Feature179,Part__Feature180,Part__Feature181,Part__Feature182]
  Origin = -> Origin022
  Placement = pos=(77.1605,-122.725,-1.6) rot=(1,0,0;3.14159rad)
FEATURE [App::Link] _7_SensorTemperatura_kicad_sch_C_0805_2012Metric_4f3bec8a4ad3_ln_008  label="05_ExtensionPulso.kicad_sch_SensorTemperatura.kicad_sch_C_0805_2012Metric_75119aad0e11"
  LinkPlacement = pos=(76.95,-84.5962,-1.6) rot=(0.707107,-0.707107,0;3.14159rad)
  LinkedObject = -> Shape001
  Placement = pos=(76.95,-84.5962,-1.6) rot=(0.707107,-0.707107,0;3.14159rad)
FEATURE [App::Link] _7_SensorTemperatura_kicad_sch_C_0805_2012Metric_4f3bec8a4ad3_ln_009  label="04_GenVref.kicad_sch_SensorTemperatura.kicad_sch_C_0805_2012Metric_bcff3c3a8cb2"
  LinkPlacement = pos=(126.65,-100.518,-1.6) rot=(0.707107,-0.707107,0;3.14159rad)
  LinkedObject = -> Shape001
  Placement = pos=(126.65,-100.518,-1.6) rot=(0.707107,-0.707107,0;3.14159rad)
FEATURE [Part::Feature] Part__Feature183  label="BODY-SON"
  Placement = pos=(0,0,0.025) rot=(1,0,0;1.5708rad)
  shape: bbox 2 x 2 x 0.75 mm, 59 faces (baked)
FEATURE [Part::Feature] Part__Feature184  label="SOLID"
  shape: bbox 1.1 x 0.2 x 2 mm, 28 faces (baked)
FEATURE [Part::Feature] Part__Feature185  label="SOLID001"
  shape: bbox 0.3 x 0.2 x 0.25 mm, 6 faces (baked)
FEATURE [Part::Feature] Part__Feature186  label="SOLID002"
  shape: bbox 0.3 x 0.2 x 0.25 mm, 6 faces (baked)
FEATURE [Part::Feature] Part__Feature187  label="SOLID003"
  shape: bbox 0.3 x 0.2 x 0.25 mm, 6 faces (baked)
FEATURE [Part::Feature] Part__Feature188  label="SOLID004"
  shape: bbox 0.3 x 0.2 x 0.25 mm, 6 faces (baked)
FEATURE [Part::Feature] Part__Feature189  label="SOLID005"
  shape: bbox 0.3 x 0.2 x 0.25 mm, 6 faces (baked)
FEATURE [Part::Feature] Part__Feature190  label="SOLID006"
  shape: bbox 0.3 x 0.2 x 0.25 mm, 6 faces (baked)
FEATURE [Part::Feature] Part__Feature191  label="SOLID007"
  shape: bbox 0.3 x 0.2 x 0.25 mm, 6 faces (baked)
FEATURE [Part::Feature] Part__Feature192  label="SOLID008"
  shape: bbox 0.3 x 0.2 x 0.25 mm, 6 faces (baked)
FEATURE [App::Part] FRAME_DSG0008A  label="FRAME-DSG0008A"
  Group = -> [Part__Feature184,Part__Feature185,Part__Feature186,Part__Feature187,Part__Feature188,Part__Feature189,Part__Feature190,Part__Feature191,Part__Feature192]
  Origin = -> Origin023
  Placement = pos=(0,0,0) rot=(1,0,0;1.5708rad)
FEATURE [App::Part] DSG0008A_ASM  label="02_Amplificacion.kicad_sch_DSG0008A_ASM_57f97972f78b"
  Group = -> [Part__Feature183,FRAME_DSG0008A]
  Origin = -> Origin024
  Placement = pos=(83.5001,-106.472,-1.6) rot=(0.707107,0.707107,0;3.14159rad)
FEATURE [App::Link] _7_SensorTemperatura_kicad_sch_C_0805_2012Metric_4f3bec8a4ad3_ln_010  label="04_GenVref.kicad_sch_SensorTemperatura.kicad_sch_C_0805_2012Metric_2e55c9e9e7a3"
  LinkPlacement = pos=(125.55,-94.718,-1.6) rot=(0.707107,-0.707107,0;3.14159rad)
  LinkedObject = -> Shape001
  Placement = pos=(125.55,-94.718,-1.6) rot=(0.707107,-0.707107,0;3.14159rad)
FEATURE [App::Link] _4_GenVref_kicad_sch_R_0805_2012Metric_e7e7c0ed52a6_ln_011  label="05_ExtensionPulso.kicad_sch_GenVref.kicad_sch_R_0805_2012Metric_d70c889e8c59"
  LinkPlacement = pos=(103.763,-95.9788,-1.6) rot=(1,0,0;3.14159rad)
  LinkedObject = -> Shape003
  Placement = pos=(103.763,-95.9788,-1.6) rot=(1,0,0;3.14159rad)
FEATURE [Part::Feature] Part__Feature193  label="part081"
  shape: bbox 0.1499 x 0.1499 x 0.002 mm, 3 faces (baked)
FEATURE [Part::Feature] Part__Feature194  label="part082"
  shape: bbox 2.998 x 2.998 x 0.889 mm, 6 faces (baked)
FEATURE [Part::Feature] Part__Feature195  label="part083"
  shape: bbox 1.6 x 2.412 x 0.051 mm, 6 faces (baked)
FEATURE [Part::Feature] Part__Feature196  label="part084"
  shape: bbox 0.559 x 0.356 x 0.47 mm, 8 faces (baked)
FEATURE [Part::Feature] Part__Feature197  label="part085"
  shape: bbox 0.559 x 0.356 x 0.47 mm, 8 faces (baked)
FEATURE [Part::Feature] Part__Feature198  label="part086"
  shape: bbox 0.559 x 0.356 x 0.47 mm, 8 faces (baked)
FEATURE [Part::Feature] Part__Feature199  label="part087"
  shape: bbox 0.559 x 0.356 x 0.47 mm, 8 faces (baked)
FEATURE [Part::Feature] Part__Feature200  label="part088"
  shape: bbox 0.559 x 0.356 x 0.47 mm, 8 faces (baked)
FEATURE [Part::Feature] Part__Feature201  label="part089"
  shape: bbox 0.559 x 0.356 x 0.47 mm, 8 faces (baked)
FEATURE [Part::Feature] Part__Feature202  label="part090"
  shape: bbox 0.559 x 0.356 x 0.47 mm, 8 faces (baked)
FEATURE [Part::Feature] Part__Feature203  label="part091"
  shape: bbox 0.559 x 0.356 x 0.47 mm, 8 faces (baked)
FEATURE [App::Part] part003  label="04_GenVref.kicad_sch_part092_94bb9f3815f2"
  Group = -> [Part__Feature193,Part__Feature194,Part__Feature195,Part__Feature196,Part__Feature197,Part__Feature198,Part__Feature199,Part__Feature200,Part__Feature201,Part__Feature202,Part__Feature203]
  Origin = -> Origin025
  Placement = pos=(123.775,-100.84,-1.6) rot=(0.707107,0.707107,0;3.14159rad)
FEATURE [App::Link] _1_Polarizacion_kicad_sch_C_0603_1608Metric_c67edd4d6b6e_ln_  label="01_Polarizacion.kicad_sch_Polarizacion.kicad_sch_C_0603_1608Metric_377d0d437d72"
  LinkPlacement = pos=(93.675,-122.6,-1.6) rot=(0.707107,-0.707107,0;3.14159rad)
  LinkedObject = -> Shape007
  Placement = pos=(93.675,-122.6,-1.6) rot=(0.707107,-0.707107,0;3.14159rad)
FEATURE [Part::Feature] Part__Feature204  label="part092"
  shape: bbox 0.06985 x 0.06985 x 0.003 mm, 3 faces (baked)
FEATURE [Part::Feature] Part__Feature205  label="part093"
  shape: bbox 1.397 x 2.161 x 1.093 mm, 14 faces (baked)
FEATURE [Part::Feature] Part__Feature206  label="part094"
  shape: bbox 0.498 x 0.306 x 0.675 mm, 14 faces (baked)
FEATURE [Part::Feature] Part__Feature207  label="part095"
  shape: bbox 0.498 x 0.306 x 0.675 mm, 14 faces (baked)
FEATURE [Part::Feature] Part__Feature208  label="part096"
  shape: bbox 0.498 x 0.306 x 0.675 mm, 14 faces (baked)
FEATURE [Part::Feature] Part__Feature209  label="part097"
  shape: bbox 0.498 x 0.306 x 0.675 mm, 14 faces (baked)
FEATURE [Part::Feature] Part__Feature210  label="part098"
  shape: bbox 0.498 x 0.306 x 0.675 mm, 14 faces (baked)
FEATURE [App::Part] part004  label="05_ExtensionPulso.kicad_sch_part099_1e18ba8c7ab6"
  Group = -> [Part__Feature204,Part__Feature205,Part__Feature206,Part__Feature207,Part__Feature208,Part__Feature209,Part__Feature210]
  Origin = -> Origin026
  Placement = pos=(72.6,-89.4674,-1.6) rot=(0.707107,-0.707107,0;3.14159rad)
FEATURE [App::Link] _4_GenVref_kicad_sch_R_0805_2012Metric_e7e7c0ed52a6_ln_012  label="09_AdapVoltajeDigital.kicad_sch_GenVref.kicad_sch_R_0805_2012Metric_22443eea2ec5"
  LinkPlacement = pos=(63.6875,-86.2086,-1.6) rot=(0,1,0;3.14159rad)
  LinkedObject = -> Shape003
  Placement = pos=(63.6875,-86.2086,-1.6) rot=(0,1,0;3.14159rad)
FEATURE [App::Link] _9_AdapVoltajeDigital_kicad_sch_part066_f10ad10a87d3_ln_  label="09_AdapVoltajeDigital.kicad_sch_AdapVoltajeDigital.kicad_sch_part066_6fb70bc1b834"
  LinkPlacement = pos=(64.525,-81,-1.6) rot=(0.707107,-0.707107,0;3.14159rad)
  LinkedObject = -> part001
  Placement = pos=(64.525,-81,-1.6) rot=(0.707107,-0.707107,0;3.14159rad)
FEATURE [App::Link] _4_GenVref_kicad_sch_R_0805_2012Metric_e7e7c0ed52a6_ln_013  label="03_Comparación.kicad_sch_GenVref.kicad_sch_R_0805_2012Metric_3096b1cac325"
  LinkPlacement = pos=(92.2717,-88.4092,-1.6) rot=(0.707107,0.707107,0;3.14159rad)
  LinkedObject = -> Shape003
  Placement = pos=(92.2717,-88.4092,-1.6) rot=(0.707107,0.707107,0;3.14159rad)
FEATURE [App::Link] _7_SensorTemperatura_kicad_sch_C_0805_2012Metric_4f3bec8a4ad3_ln_011  label="09_AdapVoltajeDigital.kicad_sch_SensorTemperatura.kicad_sch_C_0805_2012Metric_b93b06797fd4"
  LinkPlacement = pos=(60.425,-85.65,-1.6) rot=(0.707107,-0.707107,0;3.14159rad)
  LinkedObject = -> Shape001
  Placement = pos=(60.425,-85.65,-1.6) rot=(0.707107,-0.707107,0;3.14159rad)
FEATURE [App::Link] _1_Polarizacion_kicad_sch_R_0603_1608Metric_55dffa615082_ln_  label="01_Polarizacion.kicad_sch_Polarizacion.kicad_sch_R_0603_1608Metric_87d748e844b2"
  LinkPlacement = pos=(71.725,-124.5,-1.6) rot=(0.707107,0.707107,0;3.14159rad)
  LinkedObject = -> Shape004
  Placement = pos=(71.725,-124.5,-1.6) rot=(0.707107,0.707107,0;3.14159rad)
FEATURE [App::Link] _7_SensorTemperatura_kicad_sch_C_0805_2012Metric_4f3bec8a4ad3_ln_012  label="09_AdapVoltajeDigital.kicad_sch_SensorTemperatura.kicad_sch_C_0805_2012Metric_7cd32f02eb0c"
  LinkPlacement = pos=(120.4,-132.3,-1.6) rot=(1,0,0;3.14159rad)
  LinkedObject = -> Shape001
  Placement = pos=(120.4,-132.3,-1.6) rot=(1,0,0;3.14159rad)
FEATURE [Part::Feature] Part__Feature211  label="part099"
  shape: bbox 0.108 x 0.108 x 0.002 mm, 3 faces (baked)
FEATURE [Part::Feature] Part__Feature212  label="part100"
  shape: bbox 2.16 x 2.16 x 0.559 mm, 6 faces (baked)
FEATURE [Part::Feature] Part__Feature213  label="part101"
  shape: bbox 0.458 x 1.6 x 0.051 mm, 6 faces (baked)
FEATURE [Part::Feature] Part__Feature214  label="part102"
  shape: bbox 0.432 x 0.304 x 0.305 mm, 8 faces (baked)
FEATURE [Part::Feature] Part__Feature215  label="part103"
  shape: bbox 0.432 x 0.304 x 0.305 mm, 8 faces (baked)
FEATURE [Part::Feature] Part__Feature216  label="part104"
  shape: bbox 0.432 x 0.304 x 0.305 mm, 8 faces (baked)
FEATURE [Part::Feature] Part__Feature217  label="part105"
  shape: bbox 0.432 x 0.304 x 0.305 mm, 8 faces (baked)
FEATURE [Part::Feature] Part__Feature218  label="part106"
  shape: bbox 0.432 x 0.304 x 0.305 mm, 8 faces (baked)
FEATURE [Part::Feature] Part__Feature219  label="part107"
  shape: bbox 0.432 x 0.304 x 0.305 mm, 8 faces (baked)
FEATURE [Part::Feature] Part__Feature220  label="part108"
  shape: bbox 0.432 x 0.304 x 0.305 mm, 8 faces (baked)
FEATURE [Part::Feature] Part__Feature221  label="part109"
  shape: bbox 0.432 x 0.304 x 0.305 mm, 8 faces (baked)
FEATURE [App::Part] part005  label="04_GenVref.kicad_sch_part110_0b65658de655"
  Group = -> [Part__Feature211,Part__Feature212,Part__Feature213,Part__Feature214,Part__Feature215,Part__Feature216,Part__Feature217,Part__Feature218,Part__Feature219,Part__Feature220,Part__Feature221]
  Origin = -> Origin027
  Placement = pos=(60.666,-116.7,-1.6) rot=(0,1,0;3.14159rad)
FEATURE [App::Link] _7_SensorTemperatura_kicad_sch_C_0805_2012Metric_4f3bec8a4ad3_ln_013  label="05_ExtensionPulso.kicad_sch_SensorTemperatura.kicad_sch_C_0805_2012Metric_16ae6ca4e98c"
  LinkPlacement = pos=(75,-80.8462,-1.6) rot=(0,1,0;3.14159rad)
  LinkedObject = -> Shape001
  Placement = pos=(75,-80.8462,-1.6) rot=(0,1,0;3.14159rad)
FEATURE [App::Link] _1_Polarizacion_kicad_sch_R_0603_1608Metric_55dffa615082_ln_001  label="01_Polarizacion.kicad_sch_Polarizacion.kicad_sch_R_0603_1608Metric_5b352e1b5e06"
  LinkPlacement = pos=(74.075,-132.3,-1.6) rot=(1,0,0;3.14159rad)
  LinkedObject = -> Shape004
  Placement = pos=(74.075,-132.3,-1.6) rot=(1,0,0;3.14159rad)
FEATURE [App::Link] _7_SensorTemperatura_kicad_sch_C_0805_2012Metric_4f3bec8a4ad3_ln_014  label="08_MedicionCorriente.kicad_sch_SensorTemperatura.kicad_sch_C_0805_2012Metric_8dee5ab16994"
  LinkPlacement = pos=(121.325,-90.8,-1.6) rot=(1,0,0;3.14159rad)
  LinkedObject = -> Shape001
  Placement = pos=(121.325,-90.8,-1.6) rot=(1,0,0;3.14159rad)
FEATURE [App::Link] _1_Polarizacion_kicad_sch_part081_0638eee03de4_ln_  label="01_Polarizacion.kicad_sch_Polarizacion.kicad_sch_part081_9e2737b78b34"
  LinkPlacement = pos=(100.911,-120.825,-1.6) rot=(1,0,0;3.14159rad)
  LinkedObject = -> part002
  Placement = pos=(100.911,-120.825,-1.6) rot=(1,0,0;3.14159rad)
FEATURE [App::Link] _7_SensorTemperatura_kicad_sch_C_0805_2012Metric_4f3bec8a4ad3_ln_015  label="04_GenVref.kicad_sch_SensorTemperatura.kicad_sch_C_0805_2012Metric_5886e44a3407"
  LinkPlacement = pos=(60.7,-114.2,-1.6) rot=(1,0,0;3.14159rad)
  LinkedObject = -> Shape001
  Placement = pos=(60.7,-114.2,-1.6) rot=(1,0,0;3.14159rad)
FEATURE [App::Link] _4_GenVref_kicad_sch_R_0805_2012Metric_e7e7c0ed52a6_ln_014  label="03_Comparación.kicad_sch_GenVref.kicad_sch_R_0805_2012Metric_3270b82b8e41"
  LinkPlacement = pos=(96.2842,-92.9217,-1.6) rot=(0,1,0;3.14159rad)
  LinkedObject = -> Shape003
  Placement = pos=(96.2842,-92.9217,-1.6) rot=(0,1,0;3.14159rad)
FEATURE [App::Link] _4_GenVref_kicad_sch_R_0805_2012Metric_e7e7c0ed52a6_ln_015  label="03_Comparación.kicad_sch_GenVref.kicad_sch_R_0805_2012Metric_33ee9d32e46a"
  LinkPlacement = pos=(83.4,-98.3,-1.6) rot=(0.707107,0.707107,0;3.14159rad)
  LinkedObject = -> Shape003
  Placement = pos=(83.4,-98.3,-1.6) rot=(0.707107,0.707107,0;3.14159rad)
FEATURE [App::Link] _7_SensorTemperatura_kicad_sch_C_0805_2012Metric_4f3bec8a4ad3_ln_016  label="01_Polarizacion.kicad_sch_SensorTemperatura.kicad_sch_C_0805_2012Metric_723fa919f4c1"
  LinkPlacement = pos=(78.8,-136.95,-1.6) rot=(1,0,0;3.14159rad)
  LinkedObject = -> Shape001
  Placement = pos=(78.8,-136.95,-1.6) rot=(1,0,0;3.14159rad)
FEATURE [App::Link] _1_Polarizacion_kicad_sch_MUA08A_ASM_555f9891b5ac_ln_  label="01_Polarizacion.kicad_sch_Polarizacion.kicad_sch_MUA08A_ASM_e9cd949d0871"
  LinkPlacement = pos=(101.787,-132.225,-1.6) rot=(1,0,0;3.14159rad)
  LinkedObject = -> MUA08A_ASM
  Placement = pos=(101.787,-132.225,-1.6) rot=(1,0,0;3.14159rad)
FEATURE [App::Link] _4_GenVref_kicad_sch_R_0805_2012Metric_e7e7c0ed52a6_ln_016  label="03_Comparación.kicad_sch_GenVref.kicad_sch_R_0805_2012Metric_6877350ee7a3"
  LinkPlacement = pos=(82.25,-92.8592,-1.6) rot=(0.707107,0.707107,0;3.14159rad)
  LinkedObject = -> Shape003
  Placement = pos=(82.25,-92.8592,-1.6) rot=(0.707107,0.707107,0;3.14159rad)
FEATURE [Part::Feature] Part__Feature222  label="part110"
  shape: bbox 0.1029 x 0.1029 x 0.002 mm, 3 faces (baked)
FEATURE [Part::Feature] Part__Feature223  label="part111"
  shape: bbox 2.058 x 2.058 x 0.762 mm, 6 faces (baked)
FEATURE [Part::Feature] Part__Feature224  label="part112"
  shape: bbox 0.99 x 1.702 x 0.051 mm, 6 faces (baked)
FEATURE [Part::Feature] Part__Feature225  label="part113"
  shape: bbox 0.356 x 0.304 x 0.406 mm, 8 faces (baked)
FEATURE [Part::Feature] Part__Feature226  label="part114"
  shape: bbox 0.356 x 0.304 x 0.406 mm, 8 faces (baked)
FEATURE [Part::Feature] Part__Feature227  label="part115"
  shape: bbox 0.356 x 0.304 x 0.406 mm, 8 faces (baked)
FEATURE [Part::Feature] Part__Feature228  label="part116"
  shape: bbox 0.356 x 0.304 x 0.406 mm, 8 faces (baked)
FEATURE [Part::Feature] Part__Feature229  label="part117"
  shape: bbox 0.356 x 0.304 x 0.406 mm, 8 faces (baked)
FEATURE [Part::Feature] Part__Feature230  label="part118"
  shape: bbox 0.356 x 0.304 x 0.406 mm, 8 faces (baked)
FEATURE [Part::Feature] Part__Feature231  label="part119"
  shape: bbox 0.356 x 0.304 x 0.406 mm, 8 faces (baked)
FEATURE [Part::Feature] Part__Feature232  label="part120"
  shape: bbox 0.356 x 0.304 x 0.406 mm, 8 faces (baked)
FEATURE [App::Part] part006  label="03_Comparación.kicad_sch_part121_1eafd4a0765f"
  Group = -> [Part__Feature222,Part__Feature223,Part__Feature224,Part__Feature225,Part__Feature226,Part__Feature227,Part__Feature228,Part__Feature229,Part__Feature230,Part__Feature231,Part__Feature232]
  Origin = -> Origin028
  Placement = pos=(94.7217,-90.025,-1.6) rot=(0.707107,0.707107,0;3.14159rad)
FEATURE [App::Link] _4_GenVref_kicad_sch_R_0805_2012Metric_e7e7c0ed52a6_ln_017  label="04_GenVref.kicad_sch_GenVref.kicad_sch_R_0805_2012Metric_ad12786016aa"
  LinkPlacement = pos=(64.05,-116.438,-1.6) rot=(0.707107,-0.707107,0;3.14159rad)
  LinkedObject = -> Shape003
  Placement = pos=(64.05,-116.438,-1.6) rot=(0.707107,-0.707107,0;3.14159rad)
FEATURE [App::Link] _4_GenVref_kicad_sch_R_0805_2012Metric_e7e7c0ed52a6_ln_018  label="04_GenVref.kicad_sch_GenVref.kicad_sch_R_0805_2012Metric_82f41cffb9c5"
  LinkPlacement = pos=(61.0625,-119.2,-1.6) rot=(0,1,0;3.14159rad)
  LinkedObject = -> Shape003
  Placement = pos=(61.0625,-119.2,-1.6) rot=(0,1,0;3.14159rad)
FEATURE [App::Link] _1_Polarizacion_kicad_sch_R_0603_1608Metric_55dffa615082_ln_002  label="01_Polarizacion.kicad_sch_Polarizacion.kicad_sch_R_0603_1608Metric_1f6309ed5df5"
  LinkPlacement = pos=(82.125,-120.675,-1.6) rot=(1,0,0;3.14159rad)
  LinkedObject = -> Shape004
  Placement = pos=(82.125,-120.675,-1.6) rot=(1,0,0;3.14159rad)
FEATURE [App::Link] _4_GenVref_kicad_sch_R_0805_2012Metric_e7e7c0ed52a6_ln_019  label="08_MedicionCorriente.kicad_sch_GenVref.kicad_sch_R_0805_2012Metric_42b8563f0a1e"
  LinkPlacement = pos=(65.3147,-92.6719,-1.6) rot=(0.707107,0.707107,0;3.14159rad)
  LinkedObject = -> Shape003
  Placement = pos=(65.3147,-92.6719,-1.6) rot=(0.707107,0.707107,0;3.14159rad)
FEATURE [App::Link] _7_SensorTemperatura_kicad_sch_C_0805_2012Metric_4f3bec8a4ad3_ln_017  label="08_MedicionCorriente.kicad_sch_SensorTemperatura.kicad_sch_C_0805_2012Metric_d9559b3a91d4"
  LinkPlacement = pos=(54.8147,-101.009,-1.6) rot=(0.707107,-0.707107,0;3.14159rad)
  LinkedObject = -> Shape001
  Placement = pos=(54.8147,-101.009,-1.6) rot=(0.707107,-0.707107,0;3.14159rad)
FEATURE [App::Link] _4_GenVref_kicad_sch_R_0805_2012Metric_e7e7c0ed52a6_ln_020  label="09_AdapVoltajeDigital.kicad_sch_GenVref.kicad_sch_R_0805_2012Metric_fc7e7ce7e395"
  LinkPlacement = pos=(63.6875,-84.0086,-1.6) rot=(0,1,0;3.14159rad)
  LinkedObject = -> Shape003
  Placement = pos=(63.6875,-84.0086,-1.6) rot=(0,1,0;3.14159rad)
FEATURE [App::Link] _7_SensorTemperatura_kicad_sch_C_0805_2012Metric_4f3bec8a4ad3_ln_018  label="01_Polarizacion.kicad_sch_SensorTemperatura.kicad_sch_C_0805_2012Metric_cce1ed306186"
  LinkPlacement = pos=(71.15,-114.4,-1.6) rot=(1,0,0;3.14159rad)
  LinkedObject = -> Shape001
  Placement = pos=(71.15,-114.4,-1.6) rot=(1,0,0;3.14159rad)
FEATURE [App::Link] _7_SensorTemperatura_kicad_sch_C_0805_2012Metric_4f3bec8a4ad3_ln_019  label="03_Comparación.kicad_sch_SensorTemperatura.kicad_sch_C_0805_2012Metric_dd3db2bc50c2"
  LinkPlacement = pos=(85,-91.5717,-1.6) rot=(0,1,0;3.14159rad)
  LinkedObject = -> Shape001
  Placement = pos=(85,-91.5717,-1.6) rot=(0,1,0;3.14159rad)
FEATURE [App::Link] _4_GenVref_kicad_sch_R_0805_2012Metric_e7e7c0ed52a6_ln_021  label="01_Polarizacion.kicad_sch_GenVref.kicad_sch_R_0805_2012Metric_b5629ff8e78c"
  LinkPlacement = pos=(90.7,-120.85,-1.6) rot=(1,0,0;3.14159rad)
  LinkedObject = -> Shape003
  Placement = pos=(90.7,-120.85,-1.6) rot=(1,0,0;3.14159rad)
FEATURE [App::Link] _4_GenVref_kicad_sch_R_0805_2012Metric_e7e7c0ed52a6_ln_022  label="09_AdapVoltajeDigital.kicad_sch_GenVref.kicad_sch_R_0805_2012Metric_a5ce9ec5bd63"
  LinkPlacement = pos=(68.575,-80.9211,-1.6) rot=(0.707107,0.707107,0;3.14159rad)
  LinkedObject = -> Shape003
  Placement = pos=(68.575,-80.9211,-1.6) rot=(0.707107,0.707107,0;3.14159rad)
FEATURE [App::Link] _1_Polarizacion_kicad_sch_R_0603_1608Metric_55dffa615082_ln_003  label="01_Polarizacion.kicad_sch_Polarizacion.kicad_sch_R_0603_1608Metric_f878bf51fab8"
  LinkPlacement = pos=(95.475,-122.6,-1.6) rot=(0.707107,0.707107,0;3.14159rad)
  LinkedObject = -> Shape004
  Placement = pos=(95.475,-122.6,-1.6) rot=(0.707107,0.707107,0;3.14159rad)
FEATURE [App::Link] _4_GenVref_kicad_sch_R_0805_2012Metric_e7e7c0ed52a6_ln_023  label="09_AdapVoltajeDigital.kicad_sch_GenVref.kicad_sch_R_0805_2012Metric_5d58ee5fd994"
  LinkPlacement = pos=(111.55,-131.338,-1.6) rot=(0.707107,0.707107,0;3.14159rad)
  LinkedObject = -> Shape003
  Placement = pos=(111.55,-131.338,-1.6) rot=(0.707107,0.707107,0;3.14159rad)
FEATURE [App::Link] _7_SensorTemperatura_kicad_sch_C_0805_2012Metric_4f3bec8a4ad3_ln_020  label="03_Comparación.kicad_sch_SensorTemperatura.kicad_sch_C_0805_2012Metric_bea9cc050107"
  LinkPlacement = pos=(96.2217,-95.0217,-1.6) rot=(1,0,0;3.14159rad)
  LinkedObject = -> Shape001
  Placement = pos=(96.2217,-95.0217,-1.6) rot=(1,0,0;3.14159rad)
FEATURE [App::Link] _4_GenVref_kicad_sch_R_0805_2012Metric_e7e7c0ed52a6_ln_024  label="08_MedicionCorriente.kicad_sch_GenVref.kicad_sch_R_0805_2012Metric_8813cbe12152"
  LinkPlacement = pos=(57.4147,-106.447,-1.6) rot=(0.707107,-0.707107,0;3.14159rad)
  LinkedObject = -> Shape003
  Placement = pos=(57.4147,-106.447,-1.6) rot=(0.707107,-0.707107,0;3.14159rad)
FEATURE [App::Link] _4_GenVref_kicad_sch_part110_0b65658de655_ln_  label="08_MedicionCorriente.kicad_sch_GenVref.kicad_sch_part110_745eed0a042c"
  LinkPlacement = pos=(58.95,-94.216,-1.6) rot=(1,0,0;3.14159rad)
  LinkedObject = -> part005
  Placement = pos=(58.95,-94.216,-1.6) rot=(1,0,0;3.14159rad)
FEATURE [App::Link] _4_GenVref_kicad_sch_R_0805_2012Metric_e7e7c0ed52a6_ln_025  label="03_Comparación.kicad_sch_GenVref.kicad_sch_R_0805_2012Metric_7cc34fb34ed2"
  LinkPlacement = pos=(86.2625,-97.3717,-1.6) rot=(0,1,0;3.14159rad)
  LinkedObject = -> Shape003
  Placement = pos=(86.2625,-97.3717,-1.6) rot=(0,1,0;3.14159rad)
FEATURE [App::Link] _4_GenVref_kicad_sch_R_0805_2012Metric_e7e7c0ed52a6_ln_026  label="02_Amplificacion.kicad_sch_GenVref.kicad_sch_R_0805_2012Metric_a60f9344c819"
  LinkPlacement = pos=(80.3003,-109.919,-1.6) rot=(0,1,0;3.14159rad)
  LinkedObject = -> Shape003
  Placement = pos=(80.3003,-109.919,-1.6) rot=(0,1,0;3.14159rad)
FEATURE [App::Link] _1_Polarizacion_kicad_sch_C_0603_1608Metric_c67edd4d6b6e_ln_001  label="01_Polarizacion.kicad_sch_Polarizacion.kicad_sch_C_0603_1608Metric_8734bcb53b1a"
  LinkPlacement = pos=(69.925,-124.5,-1.6) rot=(0.707107,-0.707107,0;3.14159rad)
  LinkedObject = -> Shape007
  Placement = pos=(69.925,-124.5,-1.6) rot=(0.707107,-0.707107,0;3.14159rad)
FEATURE [App::Link] _4_GenVref_kicad_sch_R_0805_2012Metric_e7e7c0ed52a6_ln_027  label="02_Amplificacion.kicad_sch_GenVref.kicad_sch_R_0805_2012Metric_7dccb3957ba2"
  LinkPlacement = pos=(84.3003,-112.769,-1.6) rot=(1,0,0;3.14159rad)
  LinkedObject = -> Shape003
  Placement = pos=(84.3003,-112.769,-1.6) rot=(1,0,0;3.14159rad)
FEATURE [App::Link] _5_ExtensionPulso_kicad_sch_part099_1e18ba8c7ab6_ln_  label="05_ExtensionPulso.kicad_sch_ExtensionPulso.kicad_sch_part099_c91216c64a90"
  LinkPlacement = pos=(106.2,-85.2576,-1.6) rot=(0.707107,0.707107,0;3.14159rad)
  LinkedObject = -> part004
  Placement = pos=(106.2,-85.2576,-1.6) rot=(0.707107,0.707107,0;3.14159rad)
FEATURE [App::Link] _1_Polarizacion_kicad_sch_R_0603_1608Metric_55dffa615082_ln_004  label="01_Polarizacion.kicad_sch_Polarizacion.kicad_sch_R_0603_1608Metric_908aef1b5755"
  LinkPlacement = pos=(98.675,-115.35,-1.6) rot=(0.707107,0.707107,0;3.14159rad)
  LinkedObject = -> Shape004
  Placement = pos=(98.675,-115.35,-1.6) rot=(0.707107,0.707107,0;3.14159rad)
FEATURE [Part::Feature] Part__Feature233  label="SOT765 Mold body"
  Placement = pos=(-0.0103397,0.90197,2.80263) rot=(0,0,1;0rad)
  shape: bbox 2.002 x 0.725 x 2.302 mm, 69 faces (baked)
FEATURE [Part::Feature] Part__Feature234  label="SOT765 Lead"
  Placement = pos=(0.34966,0.827142,3.20263) rot=(0,-1,0;1.5708rad)
  shape: bbox 0.22 x 0.56 x 0.4395 mm, 12 faces (baked)
FEATURE [Part::Feature] Part__Feature235  label="SOT765 Lead001"
  Placement = pos=(0.84966,0.827142,3.20263) rot=(0,-1,0;1.5708rad)
  shape: bbox 0.22 x 0.56 x 0.4395 mm, 12 faces (baked)
FEATURE [Part::Feature] Part__Feature236  label="SOT765 Lead002"
  Placement = pos=(1.34966,0.827142,3.20263) rot=(0,-1,0;1.5708rad)
  shape: bbox 0.22 x 0.56 x 0.4395 mm, 12 faces (baked)
FEATURE [Part::Feature] Part__Feature237  label="SOT765 Lead003"
  Placement = pos=(1.84966,0.827142,3.20263) rot=(0,-1,0;1.5708rad)
  shape: bbox 0.22 x 0.56 x 0.4395 mm, 12 faces (baked)
FEATURE [Part::Feature] Part__Feature238  label="SOT765 Lead004"
  Placement = pos=(1.62966,0.827142,0.102631) rot=(0,1,0;1.5708rad)
  shape: bbox 0.22 x 0.56 x 0.4395 mm, 12 faces (baked)
FEATURE [Part::Feature] Part__Feature239  label="SOT765 Lead005"
  Placement = pos=(1.12966,0.827142,0.102631) rot=(0,1,0;1.5708rad)
  shape: bbox 0.22 x 0.56 x 0.4395 mm, 12 faces (baked)
FEATURE [Part::Feature] Part__Feature240  label="SOT765 Lead006"
  Placement = pos=(0.62966,0.827142,0.102631) rot=(0,1,0;1.5708rad)
  shape: bbox 0.22 x 0.56 x 0.4395 mm, 12 faces (baked)
FEATURE [Part::Feature] Part__Feature241  label="SOT765 Lead007"
  Placement = pos=(0.12966,0.827142,0.102631) rot=(0,1,0;1.5708rad)
  shape: bbox 0.22 x 0.56 x 0.4395 mm, 12 faces (baked)
FEATURE [App::Part] SOT765_1  label="05_ExtensionPulso.kicad_sch_SOT765-1_c610b25eeb40"
  Group = -> [Part__Feature233,Part__Feature234,Part__Feature235,Part__Feature236,Part__Feature237,Part__Feature238,Part__Feature239,Part__Feature240,Part__Feature241]
  Origin = -> Origin029
  Placement = pos=(103.75,-91.7288,-0.8) rot=(-1,0,0;1.5708rad)
FEATURE [App::Link] _4_GenVref_kicad_sch_R_0805_2012Metric_e7e7c0ed52a6_ln_028  label="08_MedicionCorriente.kicad_sch_GenVref.kicad_sch_R_0805_2012Metric_a1aa6a97c580"
  LinkPlacement = pos=(126.763,-88.2,-1.6) rot=(1,0,0;3.14159rad)
  LinkedObject = -> Shape003
  Placement = pos=(126.763,-88.2,-1.6) rot=(1,0,0;3.14159rad)
FEATURE [App::Link] _1_Polarizacion_kicad_sch_R_0603_1608Metric_55dffa615082_ln_005  label="01_Polarizacion.kicad_sch_Polarizacion.kicad_sch_R_0603_1608Metric_d50ca8de9c10"
  LinkPlacement = pos=(105.875,-118.775,-1.6) rot=(1,0,0;3.14159rad)
  LinkedObject = -> Shape004
  Placement = pos=(105.875,-118.775,-1.6) rot=(1,0,0;3.14159rad)
FEATURE [App::Link] _7_SensorTemperatura_kicad_sch_C_0805_2012Metric_4f3bec8a4ad3_ln_021  label="01_Polarizacion.kicad_sch_SensorTemperatura.kicad_sch_C_0805_2012Metric_9fcbaec610d1"
  LinkPlacement = pos=(101.8,-135.1,-1.6) rot=(1,0,0;3.14159rad)
  LinkedObject = -> Shape001
  Placement = pos=(101.8,-135.1,-1.6) rot=(1,0,0;3.14159rad)
FEATURE [App::Link] _4_GenVref_kicad_sch_R_0805_2012Metric_e7e7c0ed52a6_ln_029  label="05_ExtensionPulso.kicad_sch_GenVref.kicad_sch_R_0805_2012Metric_02d44a6916a2"
  LinkPlacement = pos=(73.35,-92.3462,-1.6) rot=(1,0,0;3.14159rad)
  LinkedObject = -> Shape003
  Placement = pos=(73.35,-92.3462,-1.6) rot=(1,0,0;3.14159rad)
FEATURE [App::Link] _7_SensorTemperatura_kicad_sch_C_0805_2012Metric_4f3bec8a4ad3_ln_022  label="02_Amplificacion.kicad_sch_SensorTemperatura.kicad_sch_C_0805_2012Metric_da0146491d4e"
  LinkPlacement = pos=(94.7751,-102.093,-1.6) rot=(1,0,0;3.14159rad)
  LinkedObject = -> Shape001
  Placement = pos=(94.7751,-102.093,-1.6) rot=(1,0,0;3.14159rad)
FEATURE [App::Link] _7_SensorTemperatura_kicad_sch_C_0805_2012Metric_4f3bec8a4ad3_ln_023  label="03_Comparación.kicad_sch_SensorTemperatura.kicad_sch_C_0805_2012Metric_a4d24e94fc1b"
  LinkPlacement = pos=(86.2,-99.4717,-1.6) rot=(1,0,0;3.14159rad)
  LinkedObject = -> Shape001
  Placement = pos=(86.2,-99.4717,-1.6) rot=(1,0,0;3.14159rad)
FEATURE [App::Link] _4_GenVref_kicad_sch_R_0805_2012Metric_e7e7c0ed52a6_ln_030  label="01_Polarizacion.kicad_sch_GenVref.kicad_sch_R_0805_2012Metric_9b28d168cab5"
  LinkPlacement = pos=(67.65,-120.013,-1.6) rot=(0.707107,-0.707107,0;3.14159rad)
  LinkedObject = -> Shape003
  Placement = pos=(67.65,-120.013,-1.6) rot=(0.707107,-0.707107,0;3.14159rad)
FEATURE [App::Link] _4_GenVref_kicad_sch_part110_0b65658de655_ln_001  label="04_GenVref.kicad_sch_GenVref.kicad_sch_part110_1d7efe95acaf"
  LinkPlacement = pos=(123,-94.784,-1.6) rot=(0.707107,0.707107,0;3.14159rad)
  LinkedObject = -> part005
  Placement = pos=(123,-94.784,-1.6) rot=(0.707107,0.707107,0;3.14159rad)
FEATURE [App::Link] _1_Polarizacion_kicad_sch_C_1206_3216Metric_f1471ee13c61_ln_  label="01_Polarizacion.kicad_sch_Polarizacion.kicad_sch_C_1206_3216Metric_c440844d8f1a"
  LinkPlacement = pos=(106.75,-120.775,-1.6) rot=(0,1,0;3.14159rad)
  LinkedObject = -> Shape005
  Placement = pos=(106.75,-120.775,-1.6) rot=(0,1,0;3.14159rad)
FEATURE [App::Link] _7_SensorTemperatura_kicad_sch_C_0805_2012Metric_4f3bec8a4ad3_ln_024  label="02_Amplificacion.kicad_sch_SensorTemperatura.kicad_sch_C_0805_2012Metric_022299c087be"
  LinkPlacement = pos=(102.1,-111.1,-1.6) rot=(0,1,0;3.14159rad)
  LinkedObject = -> Shape001
  Placement = pos=(102.1,-111.1,-1.6) rot=(0,1,0;3.14159rad)
FEATURE [App::Link] _4_GenVref_kicad_sch_R_0805_2012Metric_e7e7c0ed52a6_ln_031  label="08_MedicionCorriente.kicad_sch_GenVref.kicad_sch_R_0805_2012Metric_88afb1e3a43c"
  LinkPlacement = pos=(112.987,-80.3,-1.6) rot=(0,1,0;3.14159rad)
  LinkedObject = -> Shape003
  Placement = pos=(112.987,-80.3,-1.6) rot=(0,1,0;3.14159rad)
FEATURE [App::Link] _4_GenVref_kicad_sch_R_0805_2012Metric_e7e7c0ed52a6_ln_032  label="02_Amplificacion.kicad_sch_GenVref.kicad_sch_R_0805_2012Metric_e6567e01b36d"
  LinkPlacement = pos=(94.7926,-100.063,-1.6) rot=(1,0,0;3.14159rad)
  LinkedObject = -> Shape003
  Placement = pos=(94.7926,-100.063,-1.6) rot=(1,0,0;3.14159rad)
FEATURE [App::Link] _1_Polarizacion_kicad_sch_D_SOD_123_c84daf4213db_ln_  label="01_Polarizacion.kicad_sch_Polarizacion.kicad_sch_D_SOD_123_cfec7389e37c"
  LinkPlacement = pos=(75.275,-128.675,-1.6) rot=(1,0,0;3.14159rad)
  LinkedObject = -> Shape006
  Placement = pos=(75.275,-128.675,-1.6) rot=(1,0,0;3.14159rad)
FEATURE [App::Link] _7_SensorTemperatura_kicad_sch_C_0805_2012Metric_4f3bec8a4ad3_ln_025  label="02_Amplificacion.kicad_sch_SensorTemperatura.kicad_sch_C_0805_2012Metric_65447a7f0012"
  LinkPlacement = pos=(84.3003,-114.769,-1.6) rot=(1,0,0;3.14159rad)
  LinkedObject = -> Shape001
  Placement = pos=(84.3003,-114.769,-1.6) rot=(1,0,0;3.14159rad)
FEATURE [App::Link] _4_GenVref_kicad_sch_R_0805_2012Metric_e7e7c0ed52a6_ln_033  label="06_PlacasSiPM.kicad_sch_GenVref.kicad_sch_R_0805_2012Metric_b0d47a4007dc"
  LinkPlacement = pos=(53.7,-87.2125,-1.6) rot=(0.707107,0.707107,0;3.14159rad)
  LinkedObject = -> Shape003
  Placement = pos=(53.7,-87.2125,-1.6) rot=(0.707107,0.707107,0;3.14159rad)
FEATURE [App::Link] _7_SensorTemperatura_kicad_sch_C_0805_2012Metric_4f3bec8a4ad3_ln_026  label="09_AdapVoltajeDigital.kicad_sch_SensorTemperatura.kicad_sch_C_0805_2012Metric_558a5019f77a"
  LinkPlacement = pos=(120.4,-130.309,-1.6) rot=(1,0,0;3.14159rad)
  LinkedObject = -> Shape001
  Placement = pos=(120.4,-130.309,-1.6) rot=(1,0,0;3.14159rad)
FEATURE [App::Link] _7_SensorTemperatura_kicad_sch_C_0805_2012Metric_4f3bec8a4ad3_ln_027  label="01_Polarizacion.kicad_sch_SensorTemperatura.kicad_sch_C_0805_2012Metric_79b9d7ec9f46"
  LinkPlacement = pos=(75.3,-136.95,-1.6) rot=(0,1,0;3.14159rad)
  LinkedObject = -> Shape001
  Placement = pos=(75.3,-136.95,-1.6) rot=(0,1,0;3.14159rad)
FEATURE [App::Link] _4_GenVref_kicad_sch_R_0805_2012Metric_e7e7c0ed52a6_ln_034  label="08_MedicionCorriente.kicad_sch_GenVref.kicad_sch_R_0805_2012Metric_1c1c66d6041b"
  LinkPlacement = pos=(54.4147,-97.0594,-1.6) rot=(1,0,0;3.14159rad)
  LinkedObject = -> Shape003
  Placement = pos=(54.4147,-97.0594,-1.6) rot=(1,0,0;3.14159rad)
FEATURE [App::Link] _1_Polarizacion_kicad_sch_C_0603_1608Metric_c67edd4d6b6e_ln_002  label="01_Polarizacion.kicad_sch_Polarizacion.kicad_sch_C_0603_1608Metric_01af951ef0cc"
  LinkPlacement = pos=(71.725,-127.9,-1.6) rot=(0.707107,-0.707107,0;3.14159rad)
  LinkedObject = -> Shape007
  Placement = pos=(71.725,-127.9,-1.6) rot=(0.707107,-0.707107,0;3.14159rad)
FEATURE [App::Link] _7_SensorTemperatura_kicad_sch_C_0805_2012Metric_4f3bec8a4ad3_ln_028  label="02_Amplificacion.kicad_sch_SensorTemperatura.kicad_sch_C_0805_2012Metric_d0fc4e760fa5"
  LinkPlacement = pos=(94.8,-110.25,-1.6) rot=(1,0,0;3.14159rad)
  LinkedObject = -> Shape001
  Placement = pos=(94.8,-110.25,-1.6) rot=(1,0,0;3.14159rad)
FEATURE [App::Link] _4_GenVref_kicad_sch_R_0805_2012Metric_e7e7c0ed52a6_ln_035  label="02_Amplificacion.kicad_sch_GenVref.kicad_sch_R_0805_2012Metric_5a66527fed67"
  LinkPlacement = pos=(98.35,-101.95,-1.6) rot=(1,0,0;3.14159rad)
  LinkedObject = -> Shape003
  Placement = pos=(98.35,-101.95,-1.6) rot=(1,0,0;3.14159rad)
FEATURE [App::Link] _7_SensorTemperatura_kicad_sch_C_0805_2012Metric_4f3bec8a4ad3_ln_029  label="09_AdapVoltajeDigital.kicad_sch_SensorTemperatura.kicad_sch_C_0805_2012Metric_716435be677b"
  LinkPlacement = pos=(60.625,-76.9,-1.6) rot=(0.707107,-0.707107,0;3.14159rad)
  LinkedObject = -> Shape001
  Placement = pos=(60.625,-76.9,-1.6) rot=(0.707107,-0.707107,0;3.14159rad)
FEATURE [App::Link] _7_SensorTemperatura_kicad_sch_C_0805_2012Metric_4f3bec8a4ad3_ln_030  label="02_Amplificacion.kicad_sch_SensorTemperatura.kicad_sch_C_0805_2012Metric_b87bbd415e4b"
  LinkPlacement = pos=(86.0503,-106.369,-1.6) rot=(0.707107,-0.707107,0;3.14159rad)
  LinkedObject = -> Shape001
  Placement = pos=(86.0503,-106.369,-1.6) rot=(0.707107,-0.707107,0;3.14159rad)
FEATURE [App::Link] _7_SensorTemperatura_kicad_sch_C_0805_2012Metric_4f3bec8a4ad3_ln_031  label="02_Amplificacion.kicad_sch_SensorTemperatura.kicad_sch_C_0805_2012Metric_bf15bd18cb4c"
  LinkPlacement = pos=(100.2,-99.9,-1.6) rot=(0,1,0;3.14159rad)
  LinkedObject = -> Shape001
  Placement = pos=(100.2,-99.9,-1.6) rot=(0,1,0;3.14159rad)
FEATURE [App::Link] _4_GenVref_kicad_sch_R_0805_2012Metric_e7e7c0ed52a6_ln_036  label="04_GenVref.kicad_sch_GenVref.kicad_sch_R_0805_2012Metric_e13380c9df2f"
  LinkPlacement = pos=(57.85,-114.737,-1.6) rot=(0.707107,-0.707107,0;3.14159rad)
  LinkedObject = -> Shape003
  Placement = pos=(57.85,-114.737,-1.6) rot=(0.707107,-0.707107,0;3.14159rad)
FEATURE [App::Link] _1_Polarizacion_kicad_sch_part043_50eeabfdbd3f_ln_  label="04_GenVref.kicad_sch_Polarizacion.kicad_sch_part043_c88fd473e1c9"
  LinkPlacement = pos=(118.596,-101.277,-1.6) rot=(0.707107,-0.707107,0;3.14159rad)
  LinkedObject = -> part
  Placement = pos=(118.596,-101.277,-1.6) rot=(0.707107,-0.707107,0;3.14159rad)
FEATURE [App::Link] _1_Polarizacion_kicad_sch_C_1206_3216Metric_f1471ee13c61_ln_001  label="01_Polarizacion.kicad_sch_Polarizacion.kicad_sch_C_1206_3216Metric_0792a4aa511d"
  LinkPlacement = pos=(83,-122.675,-1.6) rot=(0,1,0;3.14159rad)
  LinkedObject = -> Shape005
  Placement = pos=(83,-122.675,-1.6) rot=(0,1,0;3.14159rad)
FEATURE [App::Link] _4_GenVref_kicad_sch_R_0805_2012Metric_e7e7c0ed52a6_ln_037  label="08_MedicionCorriente.kicad_sch_GenVref.kicad_sch_R_0805_2012Metric_1bc3f010a1d9"
  LinkPlacement = pos=(54.8147,-93.8719,-1.6) rot=(0.707107,0.707107,0;3.14159rad)
  LinkedObject = -> Shape003
  Placement = pos=(54.8147,-93.8719,-1.6) rot=(0.707107,0.707107,0;3.14159rad)
FEATURE [App::Link] _1_Polarizacion_kicad_sch_R_0603_1608Metric_55dffa615082_ln_006  label="01_Polarizacion.kicad_sch_Polarizacion.kicad_sch_R_0603_1608Metric_b670a5560d47"
  LinkPlacement = pos=(101.9,-115.35,-1.6) rot=(0.707107,-0.707107,0;3.14159rad)
  LinkedObject = -> Shape004
  Placement = pos=(101.9,-115.35,-1.6) rot=(0.707107,-0.707107,0;3.14159rad)
FEATURE [App::Link] _4_GenVref_kicad_sch_R_0805_2012Metric_e7e7c0ed52a6_ln_038  label="02_Amplificacion.kicad_sch_GenVref.kicad_sch_R_0805_2012Metric_98ae2756dd18"
  LinkPlacement = pos=(80.3178,-105.849,-1.6) rot=(0,1,0;3.14159rad)
  LinkedObject = -> Shape003
  Placement = pos=(80.3178,-105.849,-1.6) rot=(0,1,0;3.14159rad)
FEATURE [App::Link] _4_GenVref_kicad_sch_R_0805_2012Metric_e7e7c0ed52a6_ln_039  label="02_Amplificacion.kicad_sch_GenVref.kicad_sch_R_0805_2012Metric_50dd63f23907"
  LinkPlacement = pos=(87.4503,-109.981,-1.6) rot=(0.707107,-0.707107,0;3.14159rad)
  LinkedObject = -> Shape003
  Placement = pos=(87.4503,-109.981,-1.6) rot=(0.707107,-0.707107,0;3.14159rad)
FEATURE [App::Link] _4_GenVref_kicad_sch_R_0805_2012Metric_e7e7c0ed52a6_ln_040  label="09_AdapVoltajeDigital.kicad_sch_GenVref.kicad_sch_R_0805_2012Metric_a94d198717ec"
  LinkPlacement = pos=(63.6625,-77.8086,-1.6) rot=(0,1,0;3.14159rad)
  LinkedObject = -> Shape003
  Placement = pos=(63.6625,-77.8086,-1.6) rot=(0,1,0;3.14159rad)
FEATURE [App::Link] _4_GenVref_kicad_sch_R_0805_2012Metric_e7e7c0ed52a6_ln_041  label="02_Amplificacion.kicad_sch_GenVref.kicad_sch_R_0805_2012Metric_9be5b2abd6fe"
  LinkPlacement = pos=(94.7926,-104.123,-1.6) rot=(0,1,0;3.14159rad)
  LinkedObject = -> Shape003
  Placement = pos=(94.7926,-104.123,-1.6) rot=(0,1,0;3.14159rad)
FEATURE [App::Link] _7_SensorTemperatura_kicad_sch_C_0805_2012Metric_4f3bec8a4ad3_ln_032  label="05_ExtensionPulso.kicad_sch_SensorTemperatura.kicad_sch_C_0805_2012Metric_58d80b1f3cd1"
  LinkPlacement = pos=(70.75,-85.7962,-1.6) rot=(0.707107,0.707107,0;3.14159rad)
  LinkedObject = -> Shape001
  Placement = pos=(70.75,-85.7962,-1.6) rot=(0.707107,0.707107,0;3.14159rad)
FEATURE [App::Link] _4_GenVref_kicad_sch_R_0805_2012Metric_e7e7c0ed52a6_ln_042  label="05_ExtensionPulso.kicad_sch_GenVref.kicad_sch_R_0805_2012Metric_b3f6f6ee3aee"
  LinkPlacement = pos=(105.45,-82.3788,-1.6) rot=(0,1,0;3.14159rad)
  LinkedObject = -> Shape003
  Placement = pos=(105.45,-82.3788,-1.6) rot=(0,1,0;3.14159rad)
FEATURE [App::Link] _4_GenVref_kicad_sch_R_0805_2012Metric_e7e7c0ed52a6_ln_043  label="05_ExtensionPulso.kicad_sch_GenVref.kicad_sch_R_0805_2012Metric_1f2b9ba4228d"
  LinkPlacement = pos=(73.3625,-94.3462,-1.6) rot=(1,0,0;3.14159rad)
  LinkedObject = -> Shape003
  Placement = pos=(73.3625,-94.3462,-1.6) rot=(1,0,0;3.14159rad)
FEATURE [App::Link] _3_Comparaci__n_kicad_sch_part121_1eafd4a0765f_ln_  label="03_Comparación.kicad_sch_Comparación.kicad_sch_part121_844a8964707b"
  LinkPlacement = pos=(84.7,-94.475,-1.6) rot=(0.707107,0.707107,0;3.14159rad)
  LinkedObject = -> part006
  Placement = pos=(84.7,-94.475,-1.6) rot=(0.707107,0.707107,0;3.14159rad)
FEATURE [App::Link] _4_GenVref_kicad_sch_R_0805_2012Metric_e7e7c0ed52a6_ln_044  label="01_Polarizacion.kicad_sch_GenVref.kicad_sch_R_0805_2012Metric_0eca787ff260"
  LinkPlacement = pos=(89.95,-123.6,-1.6) rot=(0.707107,0.707107,0;3.14159rad)
  LinkedObject = -> Shape003
  Placement = pos=(89.95,-123.6,-1.6) rot=(0.707107,0.707107,0;3.14159rad)
FEATURE [App::Link] _1_Polarizacion_kicad_sch_R_0603_1608Metric_55dffa615082_ln_007  label="01_Polarizacion.kicad_sch_Polarizacion.kicad_sch_R_0603_1608Metric_b9c7bb0d40c0"
  LinkPlacement = pos=(74.925,-117.25,-1.6) rot=(0.707107,0.707107,0;3.14159rad)
  LinkedObject = -> Shape004
  Placement = pos=(74.925,-117.25,-1.6) rot=(0.707107,0.707107,0;3.14159rad)
FEATURE [App::Link] _2_Amplificacion_kicad_sch_DSG0008A_ASM_57f97972f78b_ln_  label="02_Amplificacion.kicad_sch_Amplificacion.kicad_sch_DSG0008A_ASM_f97134277b03"
  LinkPlacement = pos=(97.9998,-104.753,-1.6) rot=(0.707107,0.707107,0;3.14159rad)
  LinkedObject = -> DSG0008A_ASM
  Placement = pos=(97.9998,-104.753,-1.6) rot=(0.707107,0.707107,0;3.14159rad)
FEATURE [App::Link] _4_GenVref_kicad_sch_R_0805_2012Metric_e7e7c0ed52a6_ln_045  label="02_Amplificacion.kicad_sch_GenVref.kicad_sch_R_0805_2012Metric_b4c80ec9a720"
  LinkPlacement = pos=(101.95,-108.263,-1.6) rot=(0.707107,-0.707107,0;3.14159rad)
  LinkedObject = -> Shape003
  Placement = pos=(101.95,-108.263,-1.6) rot=(0.707107,-0.707107,0;3.14159rad)
FEATURE [App::Link] _4_GenVref_kicad_sch_R_0805_2012Metric_e7e7c0ed52a6_ln_046  label="05_ExtensionPulso.kicad_sch_GenVref.kicad_sch_R_0805_2012Metric_300720f2948e"
  LinkPlacement = pos=(105.438,-80.3788,-1.6) rot=(0,1,0;3.14159rad)
  LinkedObject = -> Shape003
  Placement = pos=(105.438,-80.3788,-1.6) rot=(0,1,0;3.14159rad)
FEATURE [App::Link] _7_SensorTemperatura_kicad_sch_C_0805_2012Metric_4f3bec8a4ad3_ln_033  label="05_ExtensionPulso.kicad_sch_SensorTemperatura.kicad_sch_C_0805_2012Metric_6b9403680f9f"
  LinkPlacement = pos=(108.05,-88.9288,-1.6) rot=(0.707107,-0.707107,0;3.14159rad)
  LinkedObject = -> Shape001
  Placement = pos=(108.05,-88.9288,-1.6) rot=(0.707107,-0.707107,0;3.14159rad)
FEATURE [App::Link] _1_Polarizacion_kicad_sch_C_1206_3216Metric_f1471ee13c61_ln_002  label="01_Polarizacion.kicad_sch_Polarizacion.kicad_sch_C_1206_3216Metric_29e822de8fbe"
  LinkPlacement = pos=(71.65,-116.875,-1.6) rot=(1,0,0;3.14159rad)
  LinkedObject = -> Shape005
  Placement = pos=(71.65,-116.875,-1.6) rot=(1,0,0;3.14159rad)
FEATURE [App::Link] _7_SensorTemperatura_kicad_sch_C_0805_2012Metric_4f3bec8a4ad3_ln_034  label="02_Amplificacion.kicad_sch_SensorTemperatura.kicad_sch_C_0805_2012Metric_95746ad1d714"
  LinkPlacement = pos=(85.4503,-110.019,-1.6) rot=(0.707107,0.707107,0;3.14159rad)
  LinkedObject = -> Shape001
  Placement = pos=(85.4503,-110.019,-1.6) rot=(0.707107,0.707107,0;3.14159rad)
FEATURE [Part::Feature] Shape009  label="01_Polarizacion.kicad_sch_L_1812_4532Metric_baccccf5fdc4"
  Placement = pos=(107.075,-124.912,-1.6) rot=(0.707107,-0.707107,0;3.14159rad)
  shape: bbox 3.2 x 4.5 x 2.5 mm, 28 faces (baked)
FEATURE [App::Link] _1_Polarizacion_kicad_sch_R_0603_1608Metric_55dffa615082_ln_008  label="01_Polarizacion.kicad_sch_Polarizacion.kicad_sch_R_0603_1608Metric_38d55a5e51e8"
  LinkPlacement = pos=(107.3,-129.35,-1.6) rot=(1,0,0;3.14159rad)
  LinkedObject = -> Shape004
  Placement = pos=(107.3,-129.35,-1.6) rot=(1,0,0;3.14159rad)
FEATURE [App::Link] _7_SensorTemperatura_kicad_sch_C_0805_2012Metric_4f3bec8a4ad3_ln_035  label="05_ExtensionPulso.kicad_sch_SensorTemperatura.kicad_sch_C_0805_2012Metric_5644b2da582a"
  LinkPlacement = pos=(101.85,-90.1288,-1.6) rot=(0.707107,0.707107,0;3.14159rad)
  LinkedObject = -> Shape001
  Placement = pos=(101.85,-90.1288,-1.6) rot=(0.707107,0.707107,0;3.14159rad)
FEATURE [App::Link] _4_GenVref_kicad_sch_R_0805_2012Metric_e7e7c0ed52a6_ln_047  label="05_ExtensionPulso.kicad_sch_GenVref.kicad_sch_R_0805_2012Metric_0b9095136ad4"
  LinkPlacement = pos=(75.0375,-78.7462,-1.6) rot=(0,1,0;3.14159rad)
  LinkedObject = -> Shape003
  Placement = pos=(75.0375,-78.7462,-1.6) rot=(0,1,0;3.14159rad)
FEATURE [Part::Feature] Part__Feature242  label="BODY-SO"
  Placement = pos=(0,0,1.0033) rot=(0.57735,0.57735,0.57735;2.0944rad)
  shape: bbox 3.915 x 4.906 x 1.451 mm, 56 faces (baked)
FEATURE [Part::Feature] Part__Feature243  label="LEAD-D0008A"
  Placement = pos=(2.159,1.905,0.254) rot=(0.57735,0.57735,0.57735;2.0944rad)
  shape: bbox 1.056 x 0.4071 x 1.004 mm, 13 faces (baked)
FEATURE [Part::Feature] Part__Feature244  label="LEAD-D0008A001"
  Placement = pos=(2.159,0.635,0.254) rot=(0.57735,0.57735,0.57735;2.0944rad)
  shape: bbox 1.056 x 0.4071 x 1.004 mm, 13 faces (baked)
FEATURE [Part::Feature] Part__Feature245  label="LEAD-D0008A002"
  Placement = pos=(2.159,-0.635,0.254) rot=(0.57735,0.57735,0.57735;2.0944rad)
  shape: bbox 1.056 x 0.4071 x 1.004 mm, 13 faces (baked)
FEATURE [Part::Feature] Part__Feature246  label="LEAD-D0008A003"
  Placement = pos=(2.159,-1.905,0.254) rot=(0.57735,0.57735,0.57735;2.0944rad)
  shape: bbox 1.056 x 0.4071 x 1.004 mm, 13 faces (baked)
FEATURE [Part::Feature] Part__Feature247  label="LEAD-D0008A004"
  Placement = pos=(-2.159,1.905,0.254) rot=(0.57735,-0.57735,-0.57735;2.0944rad)
  shape: bbox 1.056 x 0.4071 x 1.004 mm, 13 faces (baked)
FEATURE [Part::Feature] Part__Feature248  label="LEAD-D0008A005"
  Placement = pos=(-2.159,0.635,0.254) rot=(0.57735,-0.57735,-0.57735;2.0944rad)
  shape: bbox 1.056 x 0.4071 x 1.004 mm, 13 faces (baked)
FEATURE [Part::Feature] Part__Feature249  label="LEAD-D0008A006"
  Placement = pos=(-2.159,-0.635,0.254) rot=(0.57735,-0.57735,-0.57735;2.0944rad)
  shape: bbox 1.056 x 0.4071 x 1.004 mm, 13 faces (baked)
FEATURE [Part::Feature] Part__Feature250  label="LEAD-D0008A007"
  Placement = pos=(-2.159,-1.905,0.254) rot=(0.57735,-0.57735,-0.57735;2.0944rad)
  shape: bbox 1.056 x 0.4071 x 1.004 mm, 13 faces (baked)
FEATURE [App::Part] D0008A_ASM  label="08_MedicionCorriente.kicad_sch_D0008A_ASM_ff69cd2c6fd6"
  Group = -> [Part__Feature242,Part__Feature243,Part__Feature244,Part__Feature245,Part__Feature246,Part__Feature247,Part__Feature248,Part__Feature249,Part__Feature250]
  Origin = -> Origin030
  Placement = pos=(58.8097,-100.881,-1.6) rot=(0.707107,0.707107,0;3.14159rad)
FEATURE [App::Link] _7_SensorTemperatura_kicad_sch_C_0805_2012Metric_4f3bec8a4ad3_ln_036  label="03_Comparación.kicad_sch_SensorTemperatura.kicad_sch_C_0805_2012Metric_a5b05f6ce53c"
  LinkPlacement = pos=(95.0217,-87.1217,-1.6) rot=(0,1,0;3.14159rad)
  LinkedObject = -> Shape001
  Placement = pos=(95.0217,-87.1217,-1.6) rot=(0,1,0;3.14159rad)
FEATURE [App::Link] _4_GenVref_kicad_sch_R_0805_2012Metric_e7e7c0ed52a6_ln_048  label="02_Amplificacion.kicad_sch_GenVref.kicad_sch_R_0805_2012Metric_f350107516de"
  LinkPlacement = pos=(98.6375,-111.05,-1.6) rot=(1,0,0;3.14159rad)
  LinkedObject = -> Shape003
  Placement = pos=(98.6375,-111.05,-1.6) rot=(1,0,0;3.14159rad)
FEATURE [App::Link] _4_GenVref_kicad_sch_R_0805_2012Metric_e7e7c0ed52a6_ln_049  label="02_Amplificacion.kicad_sch_GenVref.kicad_sch_R_0805_2012Metric_bf8a3855538a"
  LinkPlacement = pos=(91.5,-93.75,-1.6) rot=(0.707107,0.707107,0;3.14159rad)
  LinkedObject = -> Shape003
  Placement = pos=(91.5,-93.75,-1.6) rot=(0.707107,0.707107,0;3.14159rad)
FEATURE [App::Link] _4_GenVref_kicad_sch_R_0805_2012Metric_e7e7c0ed52a6_ln_050  label="02_Amplificacion.kicad_sch_GenVref.kicad_sch_R_0805_2012Metric_7091d725528c"
  LinkPlacement = pos=(94.8,-108.2,-1.6) rot=(0,1,0;3.14159rad)
  LinkedObject = -> Shape003
  Placement = pos=(94.8,-108.2,-1.6) rot=(0,1,0;3.14159rad)
FEATURE [App::Link] _1_Polarizacion_kicad_sch_R_0603_1608Metric_55dffa615082_ln_009  label="01_Polarizacion.kicad_sch_Polarizacion.kicad_sch_R_0603_1608Metric_f64e8758f55e"
  LinkPlacement = pos=(100.275,-115.35,-1.6) rot=(0.707107,-0.707107,0;3.14159rad)
  LinkedObject = -> Shape004
  Placement = pos=(100.275,-115.35,-1.6) rot=(0.707107,-0.707107,0;3.14159rad)
FEATURE [App::Link] _4_GenVref_kicad_sch_R_0805_2012Metric_e7e7c0ed52a6_ln_051  label="02_Amplificacion.kicad_sch_GenVref.kicad_sch_R_0805_2012Metric_55ed9bbd2133"
  LinkPlacement = pos=(97.95,-108.3,-1.6) rot=(0.707107,-0.707107,0;3.14159rad)
  LinkedObject = -> Shape003
  Placement = pos=(97.95,-108.3,-1.6) rot=(0.707107,-0.707107,0;3.14159rad)
FEATURE [App::Link] _7_SensorTemperatura_kicad_sch_C_0805_2012Metric_4f3bec8a4ad3_ln_037  label="08_MedicionCorriente.kicad_sch_SensorTemperatura.kicad_sch_C_0805_2012Metric_2f8cfb197d40"
  LinkPlacement = pos=(117.275,-82.35,-1.6) rot=(0.707107,0.707107,0;3.14159rad)
  LinkedObject = -> Shape001
  Placement = pos=(117.275,-82.35,-1.6) rot=(0.707107,0.707107,0;3.14159rad)
FEATURE [App::Link] _7_SensorTemperatura_kicad_sch_C_0805_2012Metric_4f3bec8a4ad3_ln_038  label="02_Amplificacion.kicad_sch_SensorTemperatura.kicad_sch_C_0805_2012Metric_8fce02a2dac0"
  LinkPlacement = pos=(80.3003,-111.969,-1.6) rot=(1,0,0;3.14159rad)
  LinkedObject = -> Shape001
  Placement = pos=(80.3003,-111.969,-1.6) rot=(1,0,0;3.14159rad)
FEATURE [App::Link] _7_SensorTemperatura_kicad_sch_C_0805_2012Metric_4f3bec8a4ad3_ln_039  label="02_Amplificacion.kicad_sch_SensorTemperatura.kicad_sch_C_0805_2012Metric_646302445440"
  LinkPlacement = pos=(80.3003,-103.819,-1.6) rot=(1,0,0;3.14159rad)
  LinkedObject = -> Shape001
  Placement = pos=(80.3003,-103.819,-1.6) rot=(1,0,0;3.14159rad)
FEATURE [App::Link] _1_Polarizacion_kicad_sch_C_0603_1608Metric_c67edd4d6b6e_ln_003  label="01_Polarizacion.kicad_sch_Polarizacion.kicad_sch_C_0603_1608Metric_9a9a240c4004"
  LinkPlacement = pos=(95.475,-125.9,-1.6) rot=(0.707107,-0.707107,0;3.14159rad)
  LinkedObject = -> Shape007
  Placement = pos=(95.475,-125.9,-1.6) rot=(0.707107,-0.707107,0;3.14159rad)
FEATURE [App::Link] _7_SensorTemperatura_kicad_sch_C_0805_2012Metric_4f3bec8a4ad3_ln_040  label="05_ExtensionPulso.kicad_sch_SensorTemperatura.kicad_sch_C_0805_2012Metric_0fc7d2e462b8"
  LinkPlacement = pos=(103.8,-93.8788,-1.6) rot=(1,0,0;3.14159rad)
  LinkedObject = -> Shape001
  Placement = pos=(103.8,-93.8788,-1.6) rot=(1,0,0;3.14159rad)
FEATURE [App::Link] _1_Polarizacion_kicad_sch_L_1812_4532Metric_baccccf5fdc4_ln_  label="01_Polarizacion.kicad_sch_Polarizacion.kicad_sch_L_1812_4532Metric_8ad00610c4a7"
  LinkPlacement = pos=(83.325,-126.812,-1.6) rot=(0.707107,-0.707107,0;3.14159rad)
  LinkedObject = -> Shape009
  Placement = pos=(83.325,-126.812,-1.6) rot=(0.707107,-0.707107,0;3.14159rad)
FEATURE [App::Link] _7_SensorTemperatura_kicad_sch_C_0805_2012Metric_4f3bec8a4ad3_ln_041  label="02_Amplificacion.kicad_sch_SensorTemperatura.kicad_sch_C_0805_2012Metric_67048baeb127"
  LinkPlacement = pos=(94.7751,-106.143,-1.6) rot=(0,1,0;3.14159rad)
  LinkedObject = -> Shape001
  Placement = pos=(94.7751,-106.143,-1.6) rot=(0,1,0;3.14159rad)
FEATURE [App::Link] _7_SensorTemperatura_kicad_sch_C_0805_2012Metric_4f3bec8a4ad3_ln_042  label="02_Amplificacion.kicad_sch_SensorTemperatura.kicad_sch_C_0805_2012Metric_ccadb6048732"
  LinkPlacement = pos=(100.525,-104.643,-1.6) rot=(0.707107,-0.707107,0;3.14159rad)
  LinkedObject = -> Shape001
  Placement = pos=(100.525,-104.643,-1.6) rot=(0.707107,-0.707107,0;3.14159rad)
FEATURE [App::Link] _4_GenVref_kicad_sch_R_0805_2012Metric_e7e7c0ed52a6_ln_052  label="08_MedicionCorriente.kicad_sch_GenVref.kicad_sch_R_0805_2012Metric_aea0ff9fd0cc"
  LinkPlacement = pos=(112.988,-82.3,-1.6) rot=(1,0,0;3.14159rad)
  LinkedObject = -> Shape003
  Placement = pos=(112.988,-82.3,-1.6) rot=(1,0,0;3.14159rad)
FEATURE [App::Link] _8_MedicionCorriente_kicad_sch_D0008A_ASM_ff69cd2c6fd6_ln_  label="08_MedicionCorriente.kicad_sch_MedicionCorriente.kicad_sch_D0008A_ASM_2e8fd4a02845"
  LinkPlacement = pos=(121.196,-86.805,-1.6) rot=(0,1,0;3.14159rad)
  LinkedObject = -> D0008A_ASM
  Placement = pos=(121.196,-86.805,-1.6) rot=(0,1,0;3.14159rad)
FEATURE [App::Link] _1_Polarizacion_kicad_sch_C_0603_1608Metric_c67edd4d6b6e_ln_004  label="01_Polarizacion.kicad_sch_Polarizacion.kicad_sch_C_0603_1608Metric_284aad9b0a60"
  LinkPlacement = pos=(82.15,-119.075,-1.6) rot=(1,0,0;3.14159rad)
  LinkedObject = -> Shape007
  Placement = pos=(82.15,-119.075,-1.6) rot=(1,0,0;3.14159rad)
FEATURE [App::Link] _4_GenVref_kicad_sch_R_0805_2012Metric_e7e7c0ed52a6_ln_053  label="08_MedicionCorriente.kicad_sch_GenVref.kicad_sch_R_0805_2012Metric_e71e07bc5ef5"
  LinkPlacement = pos=(114.188,-90.8,-1.6) rot=(0,1,0;3.14159rad)
  LinkedObject = -> Shape003
  Placement = pos=(114.188,-90.8,-1.6) rot=(0,1,0;3.14159rad)
FEATURE [App::Link] _1_Polarizacion_kicad_sch_R_0603_1608Metric_55dffa615082_ln_010  label="01_Polarizacion.kicad_sch_Polarizacion.kicad_sch_R_0603_1608Metric_4167547f1817"
  LinkPlacement = pos=(107.3,-130.85,-1.6) rot=(0,1,0;3.14159rad)
  LinkedObject = -> Shape004
  Placement = pos=(107.3,-130.85,-1.6) rot=(0,1,0;3.14159rad)
FEATURE [App::Link] _7_SensorTemperatura_kicad_sch_C_0805_2012Metric_4f3bec8a4ad3_ln_043  label="02_Amplificacion.kicad_sch_SensorTemperatura.kicad_sch_C_0805_2012Metric_2a1fcab318d0"
  LinkPlacement = pos=(99.95,-108.3,-1.6) rot=(0.707107,0.707107,0;3.14159rad)
  LinkedObject = -> Shape001
  Placement = pos=(99.95,-108.3,-1.6) rot=(0.707107,0.707107,0;3.14159rad)
FEATURE [App::Link] _4_GenVref_kicad_sch_R_0805_2012Metric_e7e7c0ed52a6_ln_054  label="04_GenVref.kicad_sch_GenVref.kicad_sch_R_0805_2012Metric_9e7fd4aff466"
  LinkPlacement = pos=(53.7625,-118.35,-1.6) rot=(0,1,0;3.14159rad)
  LinkedObject = -> Shape003
  Placement = pos=(53.7625,-118.35,-1.6) rot=(0,1,0;3.14159rad)
FEATURE [App::Link] _4_GenVref_kicad_sch_R_0805_2012Metric_e7e7c0ed52a6_ln_055  label="05_ExtensionPulso.kicad_sch_GenVref.kicad_sch_R_0805_2012Metric_1bfc9547bef9"
  LinkPlacement = pos=(102.437,-86.1788,-1.6) rot=(1,0,0;3.14159rad)
  LinkedObject = -> Shape003
  Placement = pos=(102.437,-86.1788,-1.6) rot=(1,0,0;3.14159rad)
FEATURE [App::Link] _1_Polarizacion_kicad_sch_TSOT_23_32137845036f_ln_  label="01_Polarizacion.kicad_sch_Polarizacion.kicad_sch_TSOT_23_31ac76a80dc4"
  LinkPlacement = pos=(79.525,-127.565,-1.6) rot=(0.707107,-0.707107,0;3.14159rad)
  LinkedObject = -> Shape002
  Placement = pos=(79.525,-127.565,-1.6) rot=(0.707107,-0.707107,0;3.14159rad)
FEATURE [App::Link] _4_GenVref_kicad_sch_R_0805_2012Metric_e7e7c0ed52a6_ln_056  label="09_AdapVoltajeDigital.kicad_sch_GenVref.kicad_sch_R_0805_2012Metric_c2bcc9662ca4"
  LinkPlacement = pos=(63.6625,-75.6086,-1.6) rot=(0,1,0;3.14159rad)
  LinkedObject = -> Shape003
  Placement = pos=(63.6625,-75.6086,-1.6) rot=(0,1,0;3.14159rad)
FEATURE [App::Link] _4_GenVref_kicad_sch_R_0805_2012Metric_e7e7c0ed52a6_ln_057  label="02_Amplificacion.kicad_sch_GenVref.kicad_sch_R_0805_2012Metric_4f690526bdd6"
  LinkPlacement = pos=(81.35,-98.3125,-1.6) rot=(0.707107,0.707107,0;3.14159rad)
  LinkedObject = -> Shape003
  Placement = pos=(81.35,-98.3125,-1.6) rot=(0.707107,0.707107,0;3.14159rad)
FEATURE [App::Link] _4_GenVref_kicad_sch_R_0805_2012Metric_e7e7c0ed52a6_ln_058  label="02_Amplificacion.kicad_sch_GenVref.kicad_sch_R_0805_2012Metric_d994b1cb332c"
  LinkPlacement = pos=(83.3503,-110.006,-1.6) rot=(0.707107,-0.707107,0;3.14159rad)
  LinkedObject = -> Shape003
  Placement = pos=(83.3503,-110.006,-1.6) rot=(0.707107,-0.707107,0;3.14159rad)
FEATURE [App::Link] _1_Polarizacion_kicad_sch_R_0603_1608Metric_55dffa615082_ln_011  label="01_Polarizacion.kicad_sch_Polarizacion.kicad_sch_R_0603_1608Metric_858ad7995ed0"
  LinkPlacement = pos=(74.075,-133.8,-1.6) rot=(0,1,0;3.14159rad)
  LinkedObject = -> Shape004
  Placement = pos=(74.075,-133.8,-1.6) rot=(0,1,0;3.14159rad)
FEATURE [App::Link] _1_Polarizacion_kicad_sch_R_0603_1608Metric_55dffa615082_ln_012  label="01_Polarizacion.kicad_sch_Polarizacion.kicad_sch_R_0603_1608Metric_04d059b3d32a"
  LinkPlacement = pos=(78.1,-117.25,-1.6) rot=(0.707107,-0.707107,0;3.14159rad)
  LinkedObject = -> Shape004
  Placement = pos=(78.1,-117.25,-1.6) rot=(0.707107,-0.707107,0;3.14159rad)
FEATURE [App::Link] _4_GenVref_kicad_sch_R_0805_2012Metric_e7e7c0ed52a6_ln_059  label="02_Amplificacion.kicad_sch_GenVref.kicad_sch_R_0805_2012Metric_0f4e1581d0de"
  LinkPlacement = pos=(83.9503,-103.519,-1.6) rot=(1,0,0;3.14159rad)
  LinkedObject = -> Shape003
  Placement = pos=(83.9503,-103.519,-1.6) rot=(1,0,0;3.14159rad)
FEATURE [App::Link] _4_GenVref_kicad_sch_part110_0b65658de655_ln_002  label="08_MedicionCorriente.kicad_sch_GenVref.kicad_sch_part110_338fcaf85ea3"
  LinkPlacement = pos=(114.525,-87.006,-1.6) rot=(0.707107,0.707107,0;3.14159rad)
  LinkedObject = -> part005
  Placement = pos=(114.525,-87.006,-1.6) rot=(0.707107,0.707107,0;3.14159rad)
FEATURE [App::Link] _1_Polarizacion_kicad_sch_L_1210_3225Metric_350fa5c3db90_ln_  label="01_Polarizacion.kicad_sch_Polarizacion.kicad_sch_L_1210_3225Metric_86b3767c6717"
  LinkPlacement = pos=(70.925,-120.475,-1.6) rot=(0.707107,0.707107,0;3.14159rad)
  LinkedObject = -> Shape008
  Placement = pos=(70.925,-120.475,-1.6) rot=(0.707107,0.707107,0;3.14159rad)
FEATURE [App::Link] _4_GenVref_kicad_sch_R_0805_2012Metric_e7e7c0ed52a6_ln_060  label="04_GenVref.kicad_sch_GenVref.kicad_sch_R_0805_2012Metric_c68ca7f52acd"
  LinkPlacement = pos=(119.216,-105.147,-1.6) rot=(0.707107,-0.707107,0;3.14159rad)
  LinkedObject = -> Shape003
  Placement = pos=(119.216,-105.147,-1.6) rot=(0.707107,-0.707107,0;3.14159rad)
FEATURE [App::Link] _5_ExtensionPulso_kicad_sch_SOT765_1_c610b25eeb40_ln_  label="05_ExtensionPulso.kicad_sch_ExtensionPulso.kicad_sch_SOT765-1_d179a5160022"
  LinkPlacement = pos=(75.05,-82.9962,-0.8) rot=(0,0.707107,-0.707107;3.14159rad)
  LinkedObject = -> SOT765_1
  Placement = pos=(75.05,-82.9962,-0.8) rot=(0,0.707107,-0.707107;3.14159rad)
FEATURE [App::Link] _7_SensorTemperatura_kicad_sch_C_0805_2012Metric_4f3bec8a4ad3_ln_044  label="01_Polarizacion.kicad_sch_SensorTemperatura.kicad_sch_C_0805_2012Metric_645ca0f632d5"
  LinkPlacement = pos=(94.15,-112.55,-1.6) rot=(1,0,0;3.14159rad)
  LinkedObject = -> Shape001
  Placement = pos=(94.15,-112.55,-1.6) rot=(1,0,0;3.14159rad)
FEATURE [App::Link] _4_GenVref_kicad_sch_R_0805_2012Metric_e7e7c0ed52a6_ln_061  label="01_Polarizacion.kicad_sch_GenVref.kicad_sch_R_0805_2012Metric_47c688d4b46b"
  LinkPlacement = pos=(64.1,-123.55,-1.6) rot=(0.707107,0.707107,0;3.14159rad)
  LinkedObject = -> Shape003
  Placement = pos=(64.1,-123.55,-1.6) rot=(0.707107,0.707107,0;3.14159rad)
FEATURE [App::Link] _1_Polarizacion_kicad_sch_part043_50eeabfdbd3f_ln_001  label="04_GenVref.kicad_sch_Polarizacion.kicad_sch_part043_459e301dedef"
  LinkPlacement = pos=(55.1925,-115.33,-1.6) rot=(0,1,0;3.14159rad)
  LinkedObject = -> part
  Placement = pos=(55.1925,-115.33,-1.6) rot=(0,1,0;3.14159rad)
FEATURE [App::Link] _4_GenVref_kicad_sch_R_0805_2012Metric_e7e7c0ed52a6_ln_062  label="05_ExtensionPulso.kicad_sch_GenVref.kicad_sch_R_0805_2012Metric_39d6778915a5"
  LinkPlacement = pos=(76.3625,-88.5462,-1.6) rot=(0,1,0;3.14159rad)
  LinkedObject = -> Shape003
  Placement = pos=(76.3625,-88.5462,-1.6) rot=(0,1,0;3.14159rad)
FEATURE [App::Part] Bot_d980
  Group = -> [Shape002,Shape003,Shape004,_4_GenVref_kicad_sch_R_0805_2012Metric_e7e7c0ed52a6_ln_,MUA08A_ASM,Shape005,_7_SensorTemperatura_kicad_sch_C_0805_2012Metric_4f3bec8a4ad3_ln_,_4_GenVref_kicad_sch_R_0805_2012Metric_e7e7c0ed52a6_ln_001,_4_GenVref_kicad_sch_R_0805_2012Metric_e7e7c0ed52a6_ln_002,_4_GenVref_kicad_sch_R_0805_2012Metric_e7e7c0ed52a6_ln_003,+155 more]
  Origin = -> Origin004
FEATURE [App::Part] Step_Models_d980
  Group = -> [Top_d980,Bot_d980]
  Origin = -> Origin002
FEATURE [Part::Feature] pads_area001  label="topPads_d980"
  Placement = pos=(0,0,0.02) rot=(0,0,1;0rad)
  shape: bbox 77 x 69.75 x 2e-07 mm, 258 faces, 0 solids (baked)
FEATURE [Part::Feature] Shape011  label="topTracks_d980"
  Placement = pos=(0,0,0.01) rot=(0,0,1;0rad)
  shape: bbox 74.7 x 70.02 x 2e-07 mm, 57 faces, 0 solids (baked)
FEATURE [Part::Feature] zones_area001  label="topZones_d980"
  Placement = pos=(0,0,0.01) rot=(0,0,1;0rad)
  shape: bbox 79.25 x 78.25 x 2e-07 mm, 2 faces, 0 solids (baked)
FEATURE [Part::Feature] pads_area003  label="botPads_d980"
  Placement = pos=(0,0,-1.62) rot=(0,0,1;0rad)
  shape: bbox 77 x 69.75 x 2e-07 mm, 722 faces, 0 solids (baked)
FEATURE [Part::Feature] Shape013  label="botTracks_d980"
  Placement = pos=(0,0,-1.61) rot=(0,0,1;0rad)
  shape: bbox 76 x 73.5 x 2e-07 mm, 256 faces, 0 solids (baked)
FEATURE [Part::Feature] zones_area003  label="botZones_d980"
  Placement = pos=(0,0,-1.61) rot=(0,0,1;0rad)
  shape: bbox 25.36 x 9.067 x 2e-07 mm, 4 faces, 0 solids (baked)
FEATURE [App::Part] Board_Geoms_d980
  Group = -> [Pcb_d980,PCB_Sketch_d980,pads_area001,Shape011,zones_area001,pads_area003,Shape013,zones_area003]
  Origin = -> Origin
FEATURE [App::Part] Board_d980  label="Placa_DetectorParticulas"
  Group = -> [Local_CS_d980,Board_Geoms_d980,Step_Models_d980]
  Origin = -> Origin001
  Placement = pos=(-50,150,0) rot=(0,0,1;0rad)
